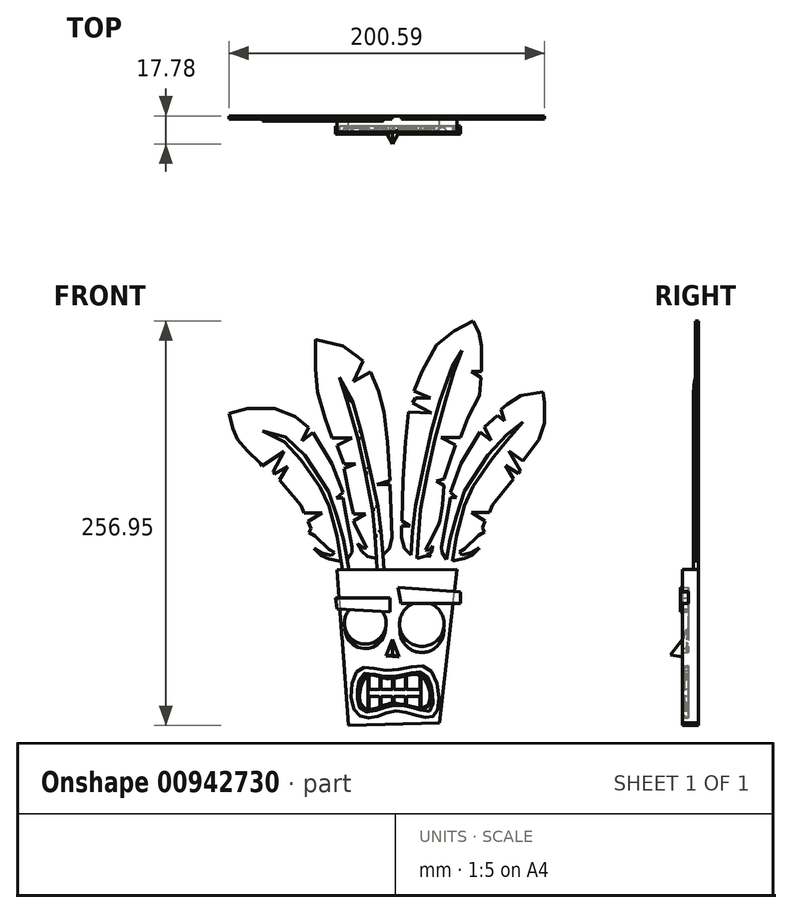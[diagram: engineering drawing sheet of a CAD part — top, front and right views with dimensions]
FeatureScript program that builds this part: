
annotation { "Feature Type Name" : "Feature", "Feature Type Description" : "" }
export const myFeature = defineFeature(function(context is Context, id is Id, definition is map)
    precondition{}
    {
        {
            var Q0;
            Q0=qCreatedBy(makeId("Front.planeOp"),FACE);
            var sketch = newSketch(context, id + "F0", { "sketchPlane" : qUnion([Q0])});
            skLineSegment(sketch, "E0", {"start": v(-33.73, 37.2) * mm, "end": v(-26.4, -61.68) * mm});
            skLineSegment(sketch, "E1", {"start": v(-26.4, -61.68) * mm, "end": v(31.35, -60.14) * mm});
            skLineSegment(sketch, "E2", {"start": v(31.35, -60.14) * mm, "end": v(42.47, 37.45) * mm});
            skLineSegment(sketch, "E3", {"start": v(42.47, 37.45) * mm, "end": v(-33.73, 37.2) * mm});
            skLineSegment(sketch, "E4", {"start": v(-30.1, 37.2) * mm, "end": v(-33.73, 58.64) * mm});
            skLineSegment(sketch, "E5", {"start": v(-33.73, 58.64) * mm, "end": v(-38.83, 77.73) * mm});
            skLineSegment(sketch, "E6", {"start": v(-38.83, 77.73) * mm, "end": v(-44.28, 90.01) * mm});
            skLineSegment(sketch, "E7", {"start": v(-44.28, 90.01) * mm, "end": v(-56.65, 107.1) * mm});
            skLineSegment(sketch, "E8", {"start": v(-56.65, 107.1) * mm, "end": v(-66.9, 118.54) * mm});
            skLineSegment(sketch, "E9", {"start": v(-66.9, 118.54) * mm, "end": v(-81.04, 125.42) * mm});
            skLineSegment(sketch, "E10", {"start": v(-81.04, 125.42) * mm, "end": v(-66.21, 121.7) * mm});
            skLineSegment(sketch, "E11", {"start": v(-66.21, 121.7) * mm, "end": v(-54.1, 109.86) * mm});
            skLineSegment(sketch, "E12", {"start": v(-54.1, 109.86) * mm, "end": v(-38.9, 87.13) * mm});
            skLineSegment(sketch, "E13", {"start": v(-38.9, 87.13) * mm, "end": v(-33.73, 71.19) * mm});
            skLineSegment(sketch, "E14", {"start": v(-33.73, 71.19) * mm, "end": v(-29.55, 56.46) * mm});
            skLineSegment(sketch, "E15", {"start": v(-29.55, 56.46) * mm, "end": v(-26, 37.22) * mm});
            skLineSegment(sketch, "E16", {"start": v(-33.73, 37.2) * mm, "end": v(42.47, 37.45) * mm, "construction": true});
            skLineSegment(sketch, "E17", {"start": v(4.37, 37.32) * mm, "end": v(4.14, 105.65) * mm, "construction": true});
            skLineSegment(sketch, "E18", {"start": v(-8.16, 37.28) * mm, "end": v(-9.36, 58.73) * mm});
            skLineSegment(sketch, "E19", {"start": v(-9.36, 58.73) * mm, "end": v(-11.04, 75.34) * mm});
            skLineSegment(sketch, "E20", {"start": v(-11.04, 75.34) * mm, "end": v(-15.42, 98.51) * mm});
            skLineSegment(sketch, "E21", {"start": v(-15.42, 98.51) * mm, "end": v(-20.28, 120.29) * mm});
            skLineSegment(sketch, "E22", {"start": v(-20.28, 120.29) * mm, "end": v(-27.17, 144.56) * mm});
            skLineSegment(sketch, "E23", {"start": v(-27.17, 144.56) * mm, "end": v(-32.03, 159.54) * mm});
            skLineSegment(sketch, "E24", {"start": v(-32.03, 159.54) * mm, "end": v(-23.71, 144.56) * mm});
            skLineSegment(sketch, "E25", {"start": v(-23.71, 144.56) * mm, "end": v(-18.3, 125.5) * mm});
            skLineSegment(sketch, "E26", {"start": v(-18.3, 125.5) * mm, "end": v(-12.9, 102.1) * mm});
            skLineSegment(sketch, "E27", {"start": v(-12.9, 102.1) * mm, "end": v(-7.76, 77.64) * mm});
            skLineSegment(sketch, "E28", {"start": v(-7.76, 77.64) * mm, "end": v(-5.82, 61.6) * mm});
            skLineSegment(sketch, "E29", {"start": v(-5.82, 61.6) * mm, "end": v(-3.76, 37.3) * mm});
            skLineSegment(sketch, "E30.MirrorCS", {"start": v(52.67, 90.34) * mm, "end": v(64.92, 107.51) * mm});
            skLineSegment(sketch, "E31.MirrorCS", {"start": v(23.74, 98.64) * mm, "end": v(28.46, 120.45) * mm});
            skLineSegment(sketch, "E32.MirrorCS", {"start": v(21.2, 102.2) * mm, "end": v(16.23, 77.72) * mm});
            skLineSegment(sketch, "E33.MirrorCS", {"start": v(17.96, 58.82) * mm, "end": v(19.52, 75.44) * mm});
            skLineSegment(sketch, "E34.MirrorCS", {"start": v(47.3, 78.02) * mm, "end": v(52.67, 90.34) * mm});
            skLineSegment(sketch, "E35.MirrorCS", {"start": v(16.23, 77.72) * mm, "end": v(14.4, 61.67) * mm});
            skLineSegment(sketch, "E36.MirrorCS", {"start": v(42.33, 58.9) * mm, "end": v(47.3, 78.02) * mm});
            skLineSegment(sketch, "E37.MirrorCS", {"start": v(19.52, 75.44) * mm, "end": v(23.74, 98.64) * mm});
            skLineSegment(sketch, "E38.MirrorCS", {"start": v(62.34, 110.25) * mm, "end": v(47.3, 87.42) * mm});
            skLineSegment(sketch, "E39.MirrorCS", {"start": v(28.46, 120.45) * mm, "end": v(35.19, 144.77) * mm});
            skLineSegment(sketch, "E40.MirrorCS", {"start": v(42.24, 71.44) * mm, "end": v(38.16, 56.68) * mm});
            skLineSegment(sketch, "E41.MirrorCS", {"start": v(31.73, 144.75) * mm, "end": v(26.45, 125.65) * mm});
            skLineSegment(sketch, "E42.MirrorCS", {"start": v(26.45, 125.65) * mm, "end": v(21.2, 102.2) * mm});
            skLineSegment(sketch, "E43.MirrorCS", {"start": v(47.3, 87.42) * mm, "end": v(42.24, 71.44) * mm});
            skLineSegment(sketch, "E44.MirrorCS", {"start": v(38.84, 37.43) * mm, "end": v(42.33, 58.9) * mm});
            skLineSegment(sketch, "E45.MirrorCS", {"start": v(38.16, 56.68) * mm, "end": v(34.74, 37.42) * mm});
            skLineSegment(sketch, "E46.MirrorCS", {"start": v(16.9, 37.36) * mm, "end": v(17.96, 58.82) * mm});
            skLineSegment(sketch, "E47.MirrorCS", {"start": v(14.4, 61.67) * mm, "end": v(12.5, 37.35) * mm});
            skLineSegment(sketch, "E48", {"start": v(-102.35, 136.45) * mm, "end": v(-99.72, 126.59) * mm});
            skLineSegment(sketch, "E49", {"start": v(-99.72, 126.59) * mm, "end": v(-96.66, 120.13) * mm});
            skLineSegment(sketch, "E50", {"start": v(-96.66, 120.13) * mm, "end": v(-90.73, 113) * mm});
            skLineSegment(sketch, "E51", {"start": v(-90.73, 113) * mm, "end": v(-82.3, 104.76) * mm});
            skLineSegment(sketch, "E52", {"start": v(-82.3, 104.76) * mm, "end": v(-81.17, 103.08) * mm});
            skLineSegment(sketch, "E53", {"start": v(-81.17, 103.08) * mm, "end": v(-67.32, 112.33) * mm});
            skLineSegment(sketch, "E54", {"start": v(-67.32, 112.33) * mm, "end": v(-74.4, 99.5) * mm});
            skLineSegment(sketch, "E55", {"start": v(-74.4, 99.5) * mm, "end": v(-73.43, 98.04) * mm});
            skLineSegment(sketch, "E56", {"start": v(-73.43, 98.04) * mm, "end": v(-65.05, 103.01) * mm});
            skLineSegment(sketch, "E57", {"start": v(-65.05, 103.01) * mm, "end": v(-70.22, 94.33) * mm});
            skLineSegment(sketch, "E58", {"start": v(-70.22, 94.33) * mm, "end": v(-56.65, 78) * mm});
            skLineSegment(sketch, "E59", {"start": v(-47.53, 58.78) * mm, "end": v(-38.6, 50.07) * mm});
            skLineSegment(sketch, "E60", {"start": v(-38.6, 50.07) * mm, "end": v(-35.37, 48.2) * mm});
            skLineSegment(sketch, "E61", {"start": v(-35.37, 48.2) * mm, "end": v(-37.05, 46.47) * mm});
            skLineSegment(sketch, "E62", {"start": v(-37.05, 46.47) * mm, "end": v(-43.38, 48.02) * mm});
            skLineSegment(sketch, "E63", {"start": v(-43.38, 48.02) * mm, "end": v(-48.26, 50.8) * mm});
            skLineSegment(sketch, "E64", {"start": v(-48.26, 50.8) * mm, "end": v(-43.68, 46.34) * mm});
            skLineSegment(sketch, "E65", {"start": v(-43.68, 46.34) * mm, "end": v(-38.6, 44.1) * mm});
            skLineSegment(sketch, "E66", {"start": v(-38.6, 44.1) * mm, "end": v(-31, 42.58) * mm});
            skLineSegment(sketch, "E67", {"start": v(-102.35, 136.45) * mm, "end": v(-90.6, 139.58) * mm});
            skLineSegment(sketch, "E68", {"start": v(-90.6, 139.58) * mm, "end": v(-73.28, 139.58) * mm});
            skLineSegment(sketch, "E69", {"start": v(-73.28, 139.58) * mm, "end": v(-60.22, 134.7) * mm});
            skLineSegment(sketch, "E70", {"start": v(-60.22, 134.7) * mm, "end": v(-51.87, 127.57) * mm});
            skLineSegment(sketch, "E71", {"start": v(-51.87, 127.57) * mm, "end": v(-55.87, 119.04) * mm});
            skLineSegment(sketch, "E72", {"start": v(-55.87, 119.04) * mm, "end": v(-48.9, 124.44) * mm});
            skLineSegment(sketch, "E73", {"start": v(-48.9, 124.44) * mm, "end": v(-36.72, 104.59) * mm});
            skLineSegment(sketch, "E74", {"start": v(-36.72, 104.59) * mm, "end": v(-29.93, 86.3) * mm});
            skLineSegment(sketch, "E75", {"start": v(-29.93, 86.3) * mm, "end": v(-33.93, 83) * mm});
            skLineSegment(sketch, "E76", {"start": v(-33.93, 83) * mm, "end": v(-29.93, 83) * mm});
            skLineSegment(sketch, "E77", {"start": v(-29.93, 83) * mm, "end": v(-28.01, 72.2) * mm});
            skLineSegment(sketch, "E78", {"start": v(-56.65, 78) * mm, "end": v(-54.63, 73.42) * mm});
            skLineSegment(sketch, "E79", {"start": v(-54.63, 73.42) * mm, "end": v(-43.22, 73.42) * mm});
            skLineSegment(sketch, "E80", {"start": v(-43.22, 73.42) * mm, "end": v(-51.93, 68.06) * mm});
            skLineSegment(sketch, "E81", {"start": v(-28.01, 72.2) * mm, "end": v(-24.22, 51.64) * mm});
            skLineSegment(sketch, "E82", {"start": v(-24.22, 51.64) * mm, "end": v(-24.22, 48.2) * mm});
            skLineSegment(sketch, "E83", {"start": v(-24.22, 48.2) * mm, "end": v(-27.16, 43.52) * mm});
            skLineSegment(sketch, "E84", {"start": v(-47.53, 58.78) * mm, "end": v(-51.56, 60.9) * mm});
            skLineSegment(sketch, "E85", {"start": v(-51.56, 60.9) * mm, "end": v(-50.22, 63.44) * mm});
            skLineSegment(sketch, "E86", {"start": v(-50.22, 63.44) * mm, "end": v(-51.93, 68.06) * mm});
            skLineSegment(sketch, "E87", {"start": v(-47.14, 183.7) * mm, "end": v(-29.93, 179.4) * mm});
            skLineSegment(sketch, "E88", {"start": v(-29.93, 179.4) * mm, "end": v(-20.26, 172.55) * mm});
            skLineSegment(sketch, "E89", {"start": v(-12.5, 163.03) * mm, "end": v(-7.3, 150.76) * mm});
            skLineSegment(sketch, "E90", {"start": v(-3.73, 137.4) * mm, "end": v(-1.54, 118.4) * mm});
            skLineSegment(sketch, "E91", {"start": v(-1.54, 118.4) * mm, "end": v(0, 94.08) * mm});
            skLineSegment(sketch, "E92", {"start": v(0, 94.08) * mm, "end": v(-8.2, 91.46) * mm});
            skLineSegment(sketch, "E93", {"start": v(-8.2, 91.46) * mm, "end": v(0, 91.46) * mm});
            skLineSegment(sketch, "E94", {"start": v(0, 91.46) * mm, "end": v(1.3, 57.73) * mm});
            skLineSegment(sketch, "E95", {"start": v(1.3, 57.73) * mm, "end": v(-0.43, 50.85) * mm});
            skLineSegment(sketch, "E96", {"start": v(-0.43, 50.85) * mm, "end": v(-4.56, 46.7) * mm});
            skLineSegment(sketch, "E97", {"start": v(-8.56, 44.51) * mm, "end": v(-14.32, 45.82) * mm});
            skLineSegment(sketch, "E98", {"start": v(-14.32, 45.82) * mm, "end": v(-17.9, 48.84) * mm});
            skLineSegment(sketch, "E99", {"start": v(-17.9, 48.84) * mm, "end": v(-20.49, 54) * mm});
            skLineSegment(sketch, "E100", {"start": v(-20.49, 54) * mm, "end": v(-16.9, 51.07) * mm});
            skLineSegment(sketch, "E101", {"start": v(-16.9, 51.07) * mm, "end": v(-14.86, 51.18) * mm});
            skLineSegment(sketch, "E102", {"start": v(-14.86, 51.18) * mm, "end": v(-18.25, 57.95) * mm});
            skLineSegment(sketch, "E103", {"start": v(-18.25, 57.95) * mm, "end": v(-22.54, 66.54) * mm});
            skLineSegment(sketch, "E104", {"start": v(-22.54, 66.54) * mm, "end": v(-23.17, 68.45) * mm});
            skLineSegment(sketch, "E105", {"start": v(-47.14, 183.7) * mm, "end": v(-47.14, 164.73) * mm});
            skLineSegment(sketch, "E106", {"start": v(-41.38, 133.7) * mm, "end": v(-36.67, 121) * mm});
            skLineSegment(sketch, "E107", {"start": v(-36.67, 121) * mm, "end": v(-24.13, 121) * mm});
            skLineSegment(sketch, "E108", {"start": v(-24.13, 121) * mm, "end": v(-33.54, 116.14) * mm});
            skLineSegment(sketch, "E109", {"start": v(-33.54, 116.14) * mm, "end": v(-29.15, 104.38) * mm});
            skLineSegment(sketch, "E110.MirrorCS", {"start": v(56.9, 51.16) * mm, "end": v(52.36, 46.66) * mm});
            skLineSegment(sketch, "E111.MirrorCS", {"start": v(32.86, 51.83) * mm, "end": v(32.89, 48.38) * mm});
            skLineSegment(sketch, "E112.MirrorCS", {"start": v(45.73, 46.75) * mm, "end": v(52.05, 48.34) * mm});
            skLineSegment(sketch, "E113.MirrorCS", {"start": v(42.37, 83.26) * mm, "end": v(38.36, 83.23) * mm});
            skLineSegment(sketch, "E114.MirrorCS", {"start": v(58.79, 63.8) * mm, "end": v(60.47, 68.44) * mm});
            skLineSegment(sketch, "E115.MirrorCS", {"start": v(52.36, 46.66) * mm, "end": v(47.3, 44.4) * mm});
            skLineSegment(sketch, "E116.MirrorCS", {"start": v(52.05, 48.34) * mm, "end": v(56.9, 51.16) * mm});
            skLineSegment(sketch, "E117.MirrorCS", {"start": v(38.34, 86.54) * mm, "end": v(42.37, 83.26) * mm});
            skLineSegment(sketch, "E118.MirrorCS", {"start": v(44.04, 48.46) * mm, "end": v(45.73, 46.75) * mm});
            skLineSegment(sketch, "E119.MirrorCS", {"start": v(65.12, 78.41) * mm, "end": v(63.13, 73.81) * mm});
            skLineSegment(sketch, "E120.MirrorCS", {"start": v(34.36, 95.01) * mm, "end": v(29.61, 93.8) * mm});
            skLineSegment(sketch, "E121.MirrorCS", {"start": v(16.2, 146.37) * mm, "end": v(14.24, 143.3) * mm});
            skLineSegment(sketch, "E122.MirrorCS", {"start": v(26.85, 58.1) * mm, "end": v(31.09, 66.72) * mm});
            skLineSegment(sketch, "E123.MirrorCS", {"start": v(64.06, 119.44) * mm, "end": v(57.06, 124.8) * mm});
            skLineSegment(sketch, "E124.MirrorCS", {"start": v(29.61, 93.8) * mm, "end": v(34.2, 90.78) * mm});
            skLineSegment(sketch, "E125.MirrorCS", {"start": v(47.25, 50.35) * mm, "end": v(44.04, 48.46) * mm});
            skLineSegment(sketch, "E126.MirrorCS", {"start": v(56.12, 59.12) * mm, "end": v(60.14, 61.28) * mm});
            skLineSegment(sketch, "E127.MirrorCS", {"start": v(82.73, 100.03) * mm, "end": v(81.76, 98.57) * mm});
            skLineSegment(sketch, "E128.MirrorCS", {"start": v(60.14, 61.28) * mm, "end": v(58.79, 63.8) * mm});
            skLineSegment(sketch, "E129.MirrorCS", {"start": v(47.3, 44.4) * mm, "end": v(39.71, 42.82) * mm});
            skLineSegment(sketch, "E130.MirrorCS", {"start": v(32.89, 48.38) * mm, "end": v(35.86, 43.73) * mm});
            skLineSegment(sketch, "E131.MirrorCS", {"start": v(9.08, 50.88) * mm, "end": v(13.23, 46.75) * mm});
            skLineSegment(sketch, "E132.MirrorCS", {"start": v(17.26, 44.6) * mm, "end": v(23, 45.95) * mm});
            skLineSegment(sketch, "E133.MirrorCS", {"start": v(31.7, 68.63) * mm, "end": v(33.27, 78.53) * mm});
            skLineSegment(sketch, "E134.MirrorCS", {"start": v(56.12, 59.12) * mm, "end": v(47.25, 50.35) * mm});
            skLineSegment(sketch, "E135.MirrorCS", {"start": v(20.39, 163.14) * mm, "end": v(15.28, 150.83) * mm});
            skLineSegment(sketch, "E136.MirrorCS", {"start": v(33.27, 78.53) * mm, "end": v(34.2, 90.78) * mm});
            skLineSegment(sketch, "E137.MirrorCS", {"start": v(15.28, 150.83) * mm, "end": v(25.86, 146.44) * mm});
            skLineSegment(sketch, "E138.MirrorCS", {"start": v(73.35, 103.48) * mm, "end": v(78.58, 94.84) * mm});
            skLineSegment(sketch, "E139.MirrorCS", {"start": v(49.47, 134) * mm, "end": v(44.85, 121.27) * mm});
            skLineSegment(sketch, "E140.MirrorCS", {"start": v(60, 127.95) * mm, "end": v(64.06, 119.44) * mm});
            skLineSegment(sketch, "E141.MirrorCS", {"start": v(32.3, 121.19) * mm, "end": v(41.75, 116.4) * mm});
            skLineSegment(sketch, "E142.MirrorCS", {"start": v(78.58, 94.84) * mm, "end": v(65.12, 78.41) * mm});
            skLineSegment(sketch, "E143.MirrorCS", {"start": v(63.13, 73.81) * mm, "end": v(51.71, 73.73) * mm});
            skLineSegment(sketch, "E144.MirrorCS", {"start": v(11.8, 137.45) * mm, "end": v(9.73, 118.45) * mm});
            skLineSegment(sketch, "E145.MirrorCS", {"start": v(37.43, 104.6) * mm, "end": v(34.36, 95.01) * mm});
            skLineSegment(sketch, "E146.MirrorCS", {"start": v(14.24, 143.3) * mm, "end": v(26.4, 136.88) * mm});
            skLineSegment(sketch, "E147.MirrorCS", {"start": v(81.76, 98.57) * mm, "end": v(73.35, 103.48) * mm});
            skLineSegment(sketch, "E148.MirrorCS", {"start": v(44.85, 121.27) * mm, "end": v(32.3, 121.19) * mm});
            skLineSegment(sketch, "E149.MirrorCS", {"start": v(51.71, 73.73) * mm, "end": v(60.47, 68.44) * mm});
            skLineSegment(sketch, "E150.MirrorCS", {"start": v(31.09, 66.72) * mm, "end": v(31.7, 68.63) * mm});
            skLineSegment(sketch, "E151.MirrorCS", {"start": v(38.36, 83.23) * mm, "end": v(36.52, 72.42) * mm});
            skLineSegment(sketch, "E152.MirrorCS", {"start": v(41.75, 116.4) * mm, "end": v(37.43, 104.6) * mm});
            skLineSegment(sketch, "E153.MirrorCS", {"start": v(36.52, 72.42) * mm, "end": v(32.86, 51.83) * mm});
            skLineSegment(sketch, "E154.MirrorCS", {"start": v(26.4, 136.88) * mm, "end": v(11.8, 137.45) * mm});
            skLineSegment(sketch, "E155.MirrorCS", {"start": v(9.73, 118.45) * mm, "end": v(8.36, 94.1) * mm});
            skLineSegment(sketch, "E156.MirrorCS", {"start": v(57.06, 124.8) * mm, "end": v(45, 104.86) * mm});
            skLineSegment(sketch, "E157.MirrorCS", {"start": v(56.71, 148.05) * mm, "end": v(49.47, 134) * mm});
            skLineSegment(sketch, "E158.MirrorCS", {"start": v(75.56, 112.81) * mm, "end": v(82.73, 100.03) * mm});
            skLineSegment(sketch, "E159.MirrorCS", {"start": v(25.86, 146.44) * mm, "end": v(16.2, 146.37) * mm});
            skLineSegment(sketch, "E160.MirrorCS", {"start": v(45, 104.86) * mm, "end": v(38.34, 86.54) * mm});
            skLineSegment(sketch, "E161.MirrorCS", {"start": v(68.3, 135.14) * mm, "end": v(60, 127.95) * mm});
            skLineSegment(sketch, "E162.MirrorCS", {"start": v(7.31, 57.75) * mm, "end": v(9.08, 50.88) * mm});
            skLineSegment(sketch, "E163", {"start": v(20.39, 163.14) * mm, "end": v(29.6, 179.9) * mm});
            skLineSegment(sketch, "E164", {"start": v(29.6, 179.9) * mm, "end": v(40.5, 188.84) * mm});
            skLineSegment(sketch, "E165", {"start": v(40.5, 188.84) * mm, "end": v(52.8, 195.27) * mm});
            skLineSegment(sketch, "E166", {"start": v(58.1, 179.34) * mm, "end": v(58.1, 163.14) * mm});
            skLineSegment(sketch, "E167", {"start": v(58.1, 163.14) * mm, "end": v(51.68, 163.14) * mm});
            skLineSegment(sketch, "E168", {"start": v(51.68, 163.14) * mm, "end": v(57.83, 159.5) * mm});
            skLineSegment(sketch, "E169", {"start": v(57.83, 159.5) * mm, "end": v(56.71, 148.05) * mm});
            skLineSegment(sketch, "E170", {"start": v(-41.38, 133.7) * mm, "end": v(-46.11, 150.28) * mm});
            skLineSegment(sketch, "E171", {"start": v(-46.11, 150.28) * mm, "end": v(-47.14, 164.73) * mm});
            skLineSegment(sketch, "E172", {"start": v(58.1, 179.34) * mm, "end": v(56.57, 188) * mm});
            skLineSegment(sketch, "E173", {"start": v(56.57, 188) * mm, "end": v(52.8, 195.27) * mm});
            skLineSegment(sketch, "E174", {"start": v(31.73, 144.75) * mm, "end": v(39.43, 166.12) * mm});
            skLineSegment(sketch, "E175", {"start": v(39.43, 166.12) * mm, "end": v(45.76, 176.67) * mm});
            skLineSegment(sketch, "E176", {"start": v(45.76, 176.67) * mm, "end": v(40.75, 163.14) * mm});
            skLineSegment(sketch, "E177", {"start": v(40.75, 163.14) * mm, "end": v(35.19, 144.77) * mm});
            skLineSegment(sketch, "E178", {"start": v(75.56, 112.81) * mm, "end": v(84.53, 106.25) * mm});
            skLineSegment(sketch, "E179", {"start": v(84.53, 106.25) * mm, "end": v(94.55, 119.94) * mm});
            skLineSegment(sketch, "E180", {"start": v(94.55, 119.94) * mm, "end": v(98.24, 130.51) * mm});
            skLineSegment(sketch, "E181", {"start": v(98.24, 130.51) * mm, "end": v(98.24, 143.43) * mm});
            skLineSegment(sketch, "E182", {"start": v(98.24, 143.43) * mm, "end": v(97.27, 150.11) * mm});
            skLineSegment(sketch, "E183", {"start": v(97.27, 150.11) * mm, "end": v(83.1, 148.05) * mm});
            skLineSegment(sketch, "E184", {"start": v(83.1, 148.05) * mm, "end": v(74.2, 142.35) * mm});
            skLineSegment(sketch, "E185", {"start": v(74.2, 142.35) * mm, "end": v(70.43, 139.02) * mm});
            skLineSegment(sketch, "E186", {"start": v(70.43, 139.02) * mm, "end": v(72.65, 131.82) * mm});
            skLineSegment(sketch, "E187", {"start": v(72.65, 131.82) * mm, "end": v(68.3, 135.14) * mm});
            skLineSegment(sketch, "E188", {"start": v(62.34, 110.25) * mm, "end": v(74.2, 123.28) * mm});
            skLineSegment(sketch, "E189", {"start": v(74.2, 123.28) * mm, "end": v(84.52, 131.04) * mm});
            skLineSegment(sketch, "E190", {"start": v(84.52, 131.04) * mm, "end": v(74.2, 119.5) * mm});
            skLineSegment(sketch, "E191", {"start": v(74.2, 119.5) * mm, "end": v(64.92, 107.51) * mm});
            skLineSegment(sketch, "E192", {"start": v(8.36, 94.1) * mm, "end": v(7.53, 68.37) * mm});
            skLineSegment(sketch, "E193", {"start": v(7.53, 68.37) * mm, "end": v(12.65, 65.19) * mm});
            skLineSegment(sketch, "E194", {"start": v(12.65, 65.19) * mm, "end": v(7.3, 65.17) * mm});
            skLineSegment(sketch, "E195", {"start": v(7.3, 65.17) * mm, "end": v(7.31, 57.75) * mm});
            skLineSegment(sketch, "E196", {"start": v(-29.15, 104.38) * mm, "end": v(-21.93, 104.38) * mm});
            skLineSegment(sketch, "E197", {"start": v(-21.93, 104.38) * mm, "end": v(-29.15, 101.63) * mm});
            skLineSegment(sketch, "E198", {"start": v(-29.15, 101.63) * mm, "end": v(-25.8, 83.95) * mm});
            skLineSegment(sketch, "E199", {"start": v(-25.8, 83.95) * mm, "end": v(-23.33, 72.63) * mm});
            skLineSegment(sketch, "E200", {"start": v(-23.33, 72.63) * mm, "end": v(-15.42, 72.63) * mm});
            skLineSegment(sketch, "E201", {"start": v(-15.42, 72.63) * mm, "end": v(-23.17, 68.45) * mm});
            skLineSegment(sketch, "E202", {"start": v(-3.73, 137.4) * mm, "end": v(-7.3, 150.76) * mm});
            skLineSegment(sketch, "E203", {"start": v(-12.5, 163.03) * mm, "end": v(-23.31, 156.9) * mm});
            skLineSegment(sketch, "E204", {"start": v(-23.31, 156.9) * mm, "end": v(-17.26, 169.77) * mm});
            skLineSegment(sketch, "E205", {"start": v(-17.26, 169.77) * mm, "end": v(-20.26, 172.55) * mm});
            skLineSegment(sketch, "E206", {"start": v(26.85, 58.1) * mm, "end": v(22.54, 49.96) * mm});
            skLineSegment(sketch, "E207", {"start": v(22.54, 49.96) * mm, "end": v(23.46, 49.47) * mm});
            skLineSegment(sketch, "E208", {"start": v(23.46, 49.47) * mm, "end": v(25.53, 50.27) * mm});
            skLineSegment(sketch, "E209", {"start": v(25.53, 50.27) * mm, "end": v(27.12, 52.37) * mm});
            skLineSegment(sketch, "E210", {"start": v(27.12, 52.37) * mm, "end": v(26.57, 48.98) * mm});
            skLineSegment(sketch, "E211", {"start": v(23, 45.95) * mm, "end": v(25.05, 45.95) * mm});
            skLineSegment(sketch, "E212", {"start": v(25.05, 45.95) * mm, "end": v(26.03, 45.66) * mm});
            skLineSegment(sketch, "E213", {"start": v(26.03, 45.66) * mm, "end": v(25.05, 46.55) * mm});
            skLineSegment(sketch, "E214", {"start": v(25.05, 46.55) * mm, "end": v(23.66, 46.98) * mm});
            skLineSegment(sketch, "E215", {"start": v(23.66, 46.98) * mm, "end": v(25.36, 47.78) * mm});
            skLineSegment(sketch, "E216", {"start": v(25.36, 47.78) * mm, "end": v(26.57, 48.98) * mm});
            skSolve(sketch);
        }
        {
            var Q0;
            Q0=makeQuery(id+"F0.imprint","IMPRINT",FACE,{"disambiguationData":[TD([[makeQuery(id+"F0.imprint","IMPRINT",EDGE,{"derivedFrom":sQuery(id+"F0.wireOp",EDGE,"E0")}),1.0]])]});
            extrude(context, id + "F1", {"entities" : qUnion([Q0]), "depth" : 6.35 * mm, "offsetDistance" : 25.4 * mm});
        }
        {
            var Q0;
            Q0=makeQuery(id+"F0.imprint","IMPRINT",FACE,{"disambiguationData":[TD([[makeQuery(id+"F0.imprint","IMPRINT",EDGE,{"derivedFrom":sQuery(id+"F0.wireOp",EDGE,"E0")}),1.0]])]});
            extrude(context, id + "F2", {"entities" : qUnion([Q0]), "depth" : 6.35 * mm, "offsetDistance" : 25.4 * mm});
        }
        {
            var Q0;
            Q0=makeQuery(id+"F1.opExtrude","CAP_FACE",FACE,{"disambiguationData":[OSD([sQuery(id+"F0.wireOp",EDGE,"E0"),sQuery(id+"F0.wireOp",EDGE,"E1"),sQuery(id+"F0.wireOp",EDGE,"E2"),sQuery(id+"F0.wireOp",EDGE,"E3")])],"isStart":false});
            var sketch = newSketch(context, id + "F3", { "sketchPlane" : qUnion([Q0])});
            skLineSegment(sketch, "E217", {"start": v(-34.59, 19.33) * mm, "end": v(0, 19.33) * mm});
            skLineSegment(sketch, "E218", {"start": v(0, 19.33) * mm, "end": v(0, 10.57) * mm});
            skLineSegment(sketch, "E219", {"start": v(0, 10.57) * mm, "end": v(-33.73, 12.37) * mm});
            skLineSegment(sketch, "E220", {"start": v(-33.73, 12.37) * mm, "end": v(-34.59, 19.33) * mm});
            skLineSegment(sketch, "E221", {"start": v(5.03, 25.97) * mm, "end": v(6.96, 15.82) * mm});
            skLineSegment(sketch, "E222", {"start": v(6.96, 15.82) * mm, "end": v(44.74, 15.82) * mm});
            skLineSegment(sketch, "E223", {"start": v(44.74, 15.82) * mm, "end": v(44.74, 23.34) * mm});
            skLineSegment(sketch, "E224", {"start": v(44.74, 23.34) * mm, "end": v(5.03, 25.97) * mm});
            skArc(sketch, "E225", {"start": v(-25.8, 11.95) * mm, "mid": v(-16.41, -9.85) * mm, "end": v(-4.77, 10.83) * mm});
            skArc(sketch, "E226", {"start": v(14.65, 15.82) * mm, "mid": v(20.25, -11.32) * mm, "end": v(25.85, 15.82) * mm});
            skArc(sketch, "E227", {"start": v(-28.5, 0) * mm, "mid": v(-15.7, -12.78) * mm, "end": v(-2.91, 0) * mm});
            skArc(sketch, "E228", {"start": v(6.39, 0) * mm, "mid": v(20.25, -15.24) * mm, "end": v(34.12, 0) * mm});
            skFitSpline(sketch, "E229", {"points": [v(-22.95, -51.39) * mm, v(-19.58, -26) * mm, v(0, -26.74) * mm, v(24.32, -25.37) * mm, v(30.05, -52.4) * mm, v(22.2, -56.35) * mm, v(3.88, -52.46) * mm, v(-11.38, -56.64) * mm, v(-22.95, -51.39) * mm]});
            skFitSpline(sketch, "E230", {"points": [v(-18.64, -47.6) * mm, v(-14.13, -30.08) * mm, v(0, -32.12) * mm, v(19.96, -30.15) * mm, v(23.88, -49.13) * mm, v(2.95, -47.38) * mm, v(-10.8, -51.39) * mm, v(-18.64, -47.6) * mm]});
            skPoint(sketch, "E231.endSnap0", {"position": v(19.13, -18.04) * mm});
            skSolve(sketch);
        }
        {
            var Q0;
            {var subQ4=sQuery(id+"F3.wireOp",EDGE,"E218");Q0=makeQuery(id+"F3.imprint","IMPRINT",FACE,{"disambiguationData":[TD([[makeQuery(id+"F3.imprint","IMPRINT",EDGE,{"derivedFrom":subQ4}),-1.0]])]});}
            var Q1;
            {var subQ0=sQuery(id+"F3.wireOp",EDGE,"E220");Q1=makeQuery(id+"F3.imprint","IMPRINT",FACE,{"disambiguationData":[TD([[makeQuery(id+"F3.imprint","IMPRINT",EDGE,{"derivedFrom":subQ0}),-1.0]])]});}
            var Q2;
            {var subQ6=sQuery(id+"F3.wireOp",EDGE,"E221");Q2=makeQuery(id+"F3.imprint","IMPRINT",FACE,{"disambiguationData":[TD([[makeQuery(id+"F3.imprint","IMPRINT",EDGE,{"derivedFrom":subQ6}),1.0]])]});}
            var Q3;
            {var subQ0=sQuery(id+"F3.wireOp",EDGE,"E223");Q3=makeQuery(id+"F3.imprint","IMPRINT",FACE,{"disambiguationData":[TD([[makeQuery(id+"F3.imprint","IMPRINT",EDGE,{"derivedFrom":subQ0}),1.0]])]});}
            extrude(context, id + "F4", {"entities" : qUnion([Q0, Q1, Q2, Q3]), "depth" : 5.08 * mm, "offsetDistance" : 25.4 * mm});
        }
        {
            var Q0;
            {var subQ0=sQuery(id+"F3.wireOp",EDGE,"E225");var subQ1=sQuery(id+"F3.wireOp",EDGE,"E219");var subQ2=makeQuery(id+"F3.imprint","INTERSECT",VERTEX,{"disambiguationData":[OD(0.0)],"derivedFrom":[subQ1,subQ0]});Q0=makeQuery(id+"F3.imprint","IMPRINT",FACE,{"disambiguationData":[TD([[makeQuery(id+"F3.imprint","IMPRINT",EDGE,{"disambiguationData":[TD([[subQ2,1.0]])],"derivedFrom":subQ1}),1.0]])]});}
            var Q1;
            {var subQ0=sQuery(id+"F3.wireOp",EDGE,"E226");var subQ1=sQuery(id+"F3.wireOp",EDGE,"E222");var subQ2=makeQuery(id+"F3.imprint","INTERSECT",VERTEX,{"disambiguationData":[OD(0.0)],"derivedFrom":[subQ1,subQ0]});Q1=makeQuery(id+"F3.imprint","IMPRINT",FACE,{"disambiguationData":[TD([[makeQuery(id+"F3.imprint","IMPRINT",EDGE,{"disambiguationData":[TD([[subQ2,-1.0]])],"derivedFrom":subQ1}),-1.0]])]});}
            extrude(context, id + "F5", {"entities" : qUnion([Q0, Q1]), "depth" : 3.8 * mm, "offsetDistance" : 25.4 * mm});
        }
        {
            var Q0;
            Q0=makeQuery(id+"F5.opExtrude","CAP_EDGE",EDGE,{"disambiguationData":[OSD([sQuery(id+"F3.wireOp",EDGE,"E226")])],"isStart":false});
            var Q1;
            Q1=makeQuery(id+"F5.opExtrude","CAP_EDGE",EDGE,{"disambiguationData":[OSD([sQuery(id+"F3.wireOp",EDGE,"E225")])],"isStart":false});
            fillet(context, id + "F6", {"entities" : qUnion([Q0, Q1]), "radius" : 3.8 * mm, "tangentPropagation" : true, "allowEdgeOverflow" : false});
        }
        {
            var Q0;
            {var subQ0=sQuery(id+"F3.wireOp",EDGE,"E227");Q0=makeQuery(id+"F3.imprint","IMPRINT",FACE,{"disambiguationData":[TD([[makeQuery(id+"F3.imprint","IMPRINT",EDGE,{"derivedFrom":subQ0}),1.0]])]});}
            var Q1;
            {var subQ0=sQuery(id+"F3.wireOp",EDGE,"E228");Q1=makeQuery(id+"F3.imprint","IMPRINT",FACE,{"disambiguationData":[TD([[makeQuery(id+"F3.imprint","IMPRINT",EDGE,{"derivedFrom":subQ0}),1.0]])]});}
            extrude(context, id + "F7", {"entities" : qUnion([Q0, Q1]), "depth" : 1.27 * mm, "offsetDistance" : 25.4 * mm});
        }
        {
            var Q0;
            Q0=makeQuery(id+"F7.opExtrude","CAP_EDGE",EDGE,{"disambiguationData":[OSD([sQuery(id+"F3.wireOp",EDGE,"E228")])],"isStart":false});
            var Q1;
            Q1=makeQuery(id+"F7.opExtrude","CAP_EDGE",EDGE,{"disambiguationData":[OSD([sQuery(id+"F3.wireOp",EDGE,"E226")])],"isStart":false});
            var Q2;
            Q2=makeQuery(id+"F7.opExtrude","CAP_EDGE",EDGE,{"disambiguationData":[OSD([sQuery(id+"F3.wireOp",EDGE,"E225")])],"isStart":false});
            var Q3;
            Q3=makeQuery(id+"F7.opExtrude","CAP_EDGE",EDGE,{"disambiguationData":[OSD([sQuery(id+"F3.wireOp",EDGE,"E227")])],"isStart":false});
            fillet(context, id + "F8", {"entities" : qUnion([Q0, Q1, Q2, Q3]), "radius" : 1.27 * mm, "tangentPropagation" : true, "allowEdgeOverflow" : false});
        }
        {
            var Q0;
            Q0=makeQuery(id+"F3.imprint","IMPRINT",FACE,{"disambiguationData":[TD([[makeQuery(id+"F3.imprint","IMPRINT",EDGE,{"derivedFrom":sQuery(id+"F3.wireOp",EDGE,"E230")}),1.0]])]});
            extrude(context, id + "F9", {"entities" : qUnion([Q0]), "depth" : 3.8 * mm, "offsetDistance" : 25.4 * mm});
        }
        {
            var Q0;
            Q0=makeQuery(id+"F9.opExtrude","CAP_EDGE",EDGE,{"disambiguationData":[OSD([sQuery(id+"F3.wireOp",EDGE,"E229")])],"isStart":false});
            fillet(context, id + "F10", {"entities" : qUnion([Q0]), "radius" : 3.8 * mm, "tangentPropagation" : true, "allowEdgeOverflow" : false});
        }
        {
            var Q0;
            Q0=makeQuery(id+"F9.opExtrude","CAP_EDGE",EDGE,{"disambiguationData":[OSD([sQuery(id+"F3.wireOp",EDGE,"E230")])],"isStart":false});
            fillet(context, id + "F11", {"entities" : qUnion([Q0]), "radius" : 0.5 * mm, "tangentPropagation" : true, "allowEdgeOverflow" : false});
        }
        {
            var Q0;
            {var subQ0=sQuery(id+"F3.wireOp",EDGE,"jRf8W3L5-f59u-6WBQ-xMSF-ZkOYL2fi1t1x");var subQ1=sQuery(id+"F3.wireOp",EDGE,"E230");var subQ2=makeQuery(id+"F3.imprint","INTERSECT",VERTEX,{"disambiguationData":[OD(0.0)],"derivedFrom":[subQ1,subQ0]});Q0=makeQuery(id+"F3.imprint","IMPRINT",FACE,{"disambiguationData":[TD([[makeQuery(id+"F3.imprint","IMPRINT",EDGE,{"disambiguationData":[TD([[subQ2,1.0]])],"derivedFrom":subQ1}),-1.0]])]});}
            var Q1;
            {var subQ0=sQuery(id+"F3.wireOp",EDGE,"NiSHTitp-dRbf-uryj-5PHh-8nDeX1NtHp2X");var subQ1=sQuery(id+"F3.wireOp",EDGE,"E230");var subQ2=makeQuery(id+"F3.imprint","INTERSECT",VERTEX,{"disambiguationData":[OD(0.0)],"derivedFrom":[subQ1,subQ0]});Q1=makeQuery(id+"F3.imprint","IMPRINT",FACE,{"disambiguationData":[TD([[makeQuery(id+"F3.imprint","IMPRINT",EDGE,{"disambiguationData":[TD([[subQ2,1.0]])],"derivedFrom":subQ1}),-1.0]])]});}
            var Q2;
            {var subQ0=sQuery(id+"F3.wireOp",EDGE,"sOFvxX6n-Jmxv-Fggd-zCcz-dTaaUDqK9s0u");var subQ1=sQuery(id+"F3.wireOp",EDGE,"E230");var subQ2=makeQuery(id+"F3.imprint","INTERSECT",VERTEX,{"disambiguationData":[OD(0.0)],"derivedFrom":[subQ1,subQ0]});Q2=makeQuery(id+"F3.imprint","IMPRINT",FACE,{"disambiguationData":[TD([[makeQuery(id+"F3.imprint","IMPRINT",EDGE,{"disambiguationData":[TD([[subQ2,1.0]])],"derivedFrom":subQ1}),-1.0]])]});}
            var Q3;
            {var subQ0=sQuery(id+"F3.wireOp",EDGE,"sOFvxX6n-Jmxv-Fggd-zCcz-dTaaUDqK9s0u");var subQ1=sQuery(id+"F3.wireOp",EDGE,"E230");var subQ2=makeQuery(id+"F3.imprint","INTERSECT",VERTEX,{"disambiguationData":[OD(0.0)],"derivedFrom":[subQ1,subQ0]});Q3=makeQuery(id+"F3.imprint","IMPRINT",FACE,{"disambiguationData":[TD([[makeQuery(id+"F3.imprint","IMPRINT",EDGE,{"disambiguationData":[TD([[subQ2,-1.0]])],"derivedFrom":subQ1}),-1.0]])]});}
            var Q4;
            {var subQ0=sQuery(id+"F3.wireOp",EDGE,"txAUoQJX-vEQ5-siAy-kIKD-OxslCe6YKnOs");var subQ1=sQuery(id+"F3.wireOp",EDGE,"E230");var subQ2=makeQuery(id+"F3.imprint","INTERSECT",VERTEX,{"disambiguationData":[OD(0.0)],"derivedFrom":[subQ1,subQ0]});Q4=makeQuery(id+"F3.imprint","IMPRINT",FACE,{"disambiguationData":[TD([[makeQuery(id+"F3.imprint","IMPRINT",EDGE,{"disambiguationData":[TD([[subQ2,-1.0]])],"derivedFrom":subQ1}),-1.0]])]});}
            var Q5;
            {var subQ0=sQuery(id+"F3.wireOp",EDGE,"cpWfK3jz-DfX8-C3p2-WDs1-wr6fSfQ65gwf");var subQ1=sQuery(id+"F3.wireOp",EDGE,"E230");var subQ2=makeQuery(id+"F3.imprint","INTERSECT",VERTEX,{"disambiguationData":[OD(0.0)],"derivedFrom":[subQ1,subQ0]});Q5=makeQuery(id+"F3.imprint","IMPRINT",FACE,{"disambiguationData":[TD([[makeQuery(id+"F3.imprint","IMPRINT",EDGE,{"disambiguationData":[TD([[subQ2,-1.0]])],"derivedFrom":subQ1}),-1.0]])]});}
            var Q6;
            {var subQ0=sQuery(id+"F3.wireOp",EDGE,"jRf8W3L5-f59u-6WBQ-xMSF-ZkOYL2fi1t1x");var subQ1=sQuery(id+"F3.wireOp",EDGE,"E230");var subQ2=makeQuery(id+"F3.imprint","INTERSECT",VERTEX,{"disambiguationData":[OD(1.0)],"derivedFrom":[subQ1,subQ0]});Q6=makeQuery(id+"F3.imprint","IMPRINT",FACE,{"disambiguationData":[TD([[makeQuery(id+"F3.imprint","IMPRINT",EDGE,{"disambiguationData":[TD([[subQ2,-1.0]])],"derivedFrom":subQ1}),-1.0]])]});}
            var Q7;
            {var subQ0=sQuery(id+"F3.wireOp",EDGE,"NiSHTitp-dRbf-uryj-5PHh-8nDeX1NtHp2X");var subQ1=sQuery(id+"F3.wireOp",EDGE,"E230");var subQ2=makeQuery(id+"F3.imprint","INTERSECT",VERTEX,{"disambiguationData":[OD(1.0)],"derivedFrom":[subQ1,subQ0]});Q7=makeQuery(id+"F3.imprint","IMPRINT",FACE,{"disambiguationData":[TD([[makeQuery(id+"F3.imprint","IMPRINT",EDGE,{"disambiguationData":[TD([[subQ2,-1.0]])],"derivedFrom":subQ1}),-1.0]])]});}
            var Q8;
            {var subQ0=sQuery(id+"F3.wireOp",EDGE,"sOFvxX6n-Jmxv-Fggd-zCcz-dTaaUDqK9s0u");var subQ1=sQuery(id+"F3.wireOp",EDGE,"E230");var subQ2=makeQuery(id+"F3.imprint","INTERSECT",VERTEX,{"disambiguationData":[OD(1.0)],"derivedFrom":[subQ1,subQ0]});Q8=makeQuery(id+"F3.imprint","IMPRINT",FACE,{"disambiguationData":[TD([[makeQuery(id+"F3.imprint","IMPRINT",EDGE,{"disambiguationData":[TD([[subQ2,-1.0]])],"derivedFrom":subQ1}),-1.0]])]});}
            var Q9;
            {var subQ0=sQuery(id+"F3.wireOp",EDGE,"sOFvxX6n-Jmxv-Fggd-zCcz-dTaaUDqK9s0u");var subQ1=sQuery(id+"F3.wireOp",EDGE,"E230");var subQ2=makeQuery(id+"F3.imprint","INTERSECT",VERTEX,{"disambiguationData":[OD(1.0)],"derivedFrom":[subQ1,subQ0]});Q9=makeQuery(id+"F3.imprint","IMPRINT",FACE,{"disambiguationData":[TD([[makeQuery(id+"F3.imprint","IMPRINT",EDGE,{"disambiguationData":[TD([[subQ2,1.0]])],"derivedFrom":subQ1}),-1.0]])]});}
            var Q10;
            {var subQ0=sQuery(id+"F3.wireOp",EDGE,"txAUoQJX-vEQ5-siAy-kIKD-OxslCe6YKnOs");var subQ1=sQuery(id+"F3.wireOp",EDGE,"E230");var subQ2=makeQuery(id+"F3.imprint","INTERSECT",VERTEX,{"disambiguationData":[OD(1.0)],"derivedFrom":[subQ1,subQ0]});Q10=makeQuery(id+"F3.imprint","IMPRINT",FACE,{"disambiguationData":[TD([[makeQuery(id+"F3.imprint","IMPRINT",EDGE,{"disambiguationData":[TD([[subQ2,1.0]])],"derivedFrom":subQ1}),-1.0]])]});}
            var Q11;
            {var subQ0=sQuery(id+"F3.wireOp",EDGE,"cpWfK3jz-DfX8-C3p2-WDs1-wr6fSfQ65gwf");var subQ1=sQuery(id+"F3.wireOp",EDGE,"E230");var subQ2=makeQuery(id+"F3.imprint","INTERSECT",VERTEX,{"disambiguationData":[OD(1.0)],"derivedFrom":[subQ1,subQ0]});Q11=makeQuery(id+"F3.imprint","IMPRINT",FACE,{"disambiguationData":[TD([[makeQuery(id+"F3.imprint","IMPRINT",EDGE,{"disambiguationData":[TD([[subQ2,1.0]])],"derivedFrom":subQ1}),-1.0]])]});}
            extrude(context, id + "F12", {"entities" : qUnion([Q0, Q1, Q2, Q3, Q4, Q5, Q6, Q7, Q8, Q9, Q10, Q11]), "depth" : 2.54 * mm, "offsetDistance" : 25.4 * mm});
        }
        {
            var Q0;
            {var subQ11=sQuery(id+"F3.wireOp",EDGE,"E218");Q0=makeQuery(id+"F3.imprint","IMPRINT",FACE,{"disambiguationData":[TD([[makeQuery(id+"F3.imprint","IMPRINT",EDGE,{"derivedFrom":subQ11}),1.0]])]});}
            cPlane(context, id + "F13", {"entities" : qUnion([Q0]), "cplaneType" : CPlaneType.OFFSET, "offset" : 11.43 * mm, "width" : 152.4 * mm, "height" : 152.4 * mm});
        }
        {
            var Q0;
            Q0=qCreatedBy(id+"F13.planeOp",FACE);
            var sketch = newSketch(context, id + "F14", { "sketchPlane" : qUnion([Q0])});
            skPoint(sketch, "E232", {"position": v(1.7, -16.89) * mm});
            skSolve(sketch);
        }
        {
            var Q0;
            {var subQ11=sQuery(id+"F3.wireOp",EDGE,"E218");Q0=makeQuery(id+"F3.imprint","IMPRINT",FACE,{"disambiguationData":[TD([[makeQuery(id+"F3.imprint","IMPRINT",EDGE,{"derivedFrom":subQ11}),1.0]])]});}
            var sketch = newSketch(context, id + "F15", { "sketchPlane" : qUnion([Q0])});
            skLineSegment(sketch, "E233", {"start": v(1.7, -2.06) * mm, "end": v(-4.5, -17.8) * mm});
            skLineSegment(sketch, "E234", {"start": v(-4.5, -17.8) * mm, "end": v(7.67, -18.63) * mm});
            skLineSegment(sketch, "E235", {"start": v(7.67, -18.63) * mm, "end": v(1.7, -2.06) * mm});
            skSolve(sketch);
        }
        {
            var Q1;
            Q1=makeQuery(id+"F15.imprint","IMPRINT",FACE,{"disambiguationData":[TD([[makeQuery(id+"F15.imprint","IMPRINT",EDGE,{"derivedFrom":sQuery(id+"F15.wireOp",EDGE,"E233")}),1.0]])]});
            var Q2;
            Q2=sQuery(id+"F14.wireOp",VERTEX,"E232");
            loft(context, id + "F16", {"operationType" : NewBodyOperationType.ADD, "sheetProfilesArray" : [{ "sheetProfileEntities" : qUnion([Q1]) }, { "sheetProfileEntities" : qUnion([Q2]) }]});
        }
        {
            var Q0;
            Q0=makeQuery(id+"F12.opExtrude","CAP_FACE",FACE,{"disambiguationData":[OSD([sQuery(id+"F3.wireOp",EDGE,"E230")])],"isStart":false});
            var sketch = newSketch(context, id + "F17", { "sketchPlane" : qUnion([Q0])});
            skLineSegment(sketch, "E236", {"start": v(-18.82, -38.83) * mm, "end": v(25, -38.83) * mm});
            skLineSegment(sketch, "E237", {"start": v(-19.3, -43.25) * mm, "end": v(25.58, -43.25) * mm});
            skLineSegment(sketch, "E238", {"start": v(1.71, -38.83) * mm, "end": v(1.71, -32.03) * mm});
            skLineSegment(sketch, "E239", {"start": v(1.71, -38.83) * mm, "end": v(1.71, -47.4) * mm});
            skLineSegment(sketch, "E240", {"start": v(2.47, -47.38) * mm, "end": v(2.47, -31.94) * mm});
            skLineSegment(sketch, "E241", {"start": v(9.9, -30.07) * mm, "end": v(9.9, -48.55) * mm});
            skLineSegment(sketch, "E242", {"start": v(10.5, -48.7) * mm, "end": v(10.5, -29.9) * mm});
            skLineSegment(sketch, "E243", {"start": v(19.14, -29.7) * mm, "end": v(19.14, -50.45) * mm});
            skLineSegment(sketch, "E244", {"start": v(19.84, -50.47) * mm, "end": v(19.84, -30.08) * mm});
            skLineSegment(sketch, "E245", {"start": v(-5.72, -30.99) * mm, "end": v(-5.72, -49.52) * mm});
            skLineSegment(sketch, "E246", {"start": v(-6.44, -30.75) * mm, "end": v(-6.44, -49.84) * mm});
            skLineSegment(sketch, "E247", {"start": v(-13.3, -29.7) * mm, "end": v(-13.3, -51.53) * mm});
            skLineSegment(sketch, "E248", {"start": v(-13.98, -30) * mm, "end": v(-13.98, -51.44) * mm});
            skSolve(sketch);
        }
        {
            var Q0;
            {var subQ0=sQuery(id+"F17.wireOp",EDGE,"E248");var subQ1=sQuery(id+"F17.wireOp",EDGE,"E236");var subQ2=makeQuery(id+"F17.imprint","INTERSECT",VERTEX,{"derivedFrom":[subQ1,subQ0]});Q0=makeQuery(id+"F17.imprint","IMPRINT",FACE,{"disambiguationData":[TD([[makeQuery(id+"F17.imprint","IMPRINT",EDGE,{"disambiguationData":[TD([[subQ2,-1.0]])],"derivedFrom":subQ1}),1.0]])]});}
            var Q1;
            {var subQ0=sQuery(id+"F17.wireOp",EDGE,"E248");var subQ1=sQuery(id+"F17.wireOp",EDGE,"E236");var subQ2=makeQuery(id+"F17.imprint","INTERSECT",VERTEX,{"derivedFrom":[subQ1,subQ0]});Q1=makeQuery(id+"F17.imprint","IMPRINT",FACE,{"disambiguationData":[TD([[makeQuery(id+"F17.imprint","IMPRINT",EDGE,{"disambiguationData":[TD([[subQ2,-1.0]])],"derivedFrom":subQ1}),-1.0]])]});}
            var Q2;
            {var subQ0=sQuery(id+"F17.wireOp",EDGE,"E247");var subQ1=sQuery(id+"F17.wireOp",EDGE,"E236");var subQ2=makeQuery(id+"F17.imprint","INTERSECT",VERTEX,{"derivedFrom":[subQ1,subQ0]});Q2=makeQuery(id+"F17.imprint","IMPRINT",FACE,{"disambiguationData":[TD([[makeQuery(id+"F17.imprint","IMPRINT",EDGE,{"disambiguationData":[TD([[subQ2,-1.0]])],"derivedFrom":subQ1}),-1.0]])]});}
            var Q3;
            {var subQ0=sQuery(id+"F17.wireOp",EDGE,"E236");var subQ1=makeQuery(id+"F12.opExtrude","CAP_EDGE",EDGE,{"disambiguationData":[OSD([sQuery(id+"F3.wireOp",EDGE,"E230")])],"isStart":false});var subQ2=makeQuery(id+"F17.imprint","INTERSECT",VERTEX,{"disambiguationData":[OD(0.0)],"derivedFrom":[subQ1,subQ0]});Q3=makeQuery(id+"F17.imprint","IMPRINT",FACE,{"disambiguationData":[TD([[makeQuery(id+"F17.imprint","IMPRINT",EDGE,{"disambiguationData":[TD([[subQ2,-1.0]])],"derivedFrom":subQ0}),-1.0]])]});}
            var Q4;
            {var subQ0=sQuery(id+"F17.wireOp",EDGE,"E248");var subQ1=sQuery(id+"F17.wireOp",EDGE,"E237");var subQ2=makeQuery(id+"F17.imprint","INTERSECT",VERTEX,{"derivedFrom":[subQ1,subQ0]});Q4=makeQuery(id+"F17.imprint","IMPRINT",FACE,{"disambiguationData":[TD([[makeQuery(id+"F17.imprint","IMPRINT",EDGE,{"disambiguationData":[TD([[subQ2,-1.0]])],"derivedFrom":subQ1}),-1.0]])]});}
            var Q5;
            {var subQ0=sQuery(id+"F17.wireOp",EDGE,"E246");var subQ1=sQuery(id+"F17.wireOp",EDGE,"E236");var subQ2=makeQuery(id+"F17.imprint","INTERSECT",VERTEX,{"derivedFrom":[subQ1,subQ0]});Q5=makeQuery(id+"F17.imprint","IMPRINT",FACE,{"disambiguationData":[TD([[makeQuery(id+"F17.imprint","IMPRINT",EDGE,{"disambiguationData":[TD([[subQ2,-1.0]])],"derivedFrom":subQ1}),-1.0]])]});}
            var Q6;
            {var subQ0=sQuery(id+"F17.wireOp",EDGE,"E246");var subQ1=sQuery(id+"F17.wireOp",EDGE,"E237");var subQ2=makeQuery(id+"F17.imprint","INTERSECT",VERTEX,{"derivedFrom":[subQ1,subQ0]});Q6=makeQuery(id+"F17.imprint","IMPRINT",FACE,{"disambiguationData":[TD([[makeQuery(id+"F17.imprint","IMPRINT",EDGE,{"disambiguationData":[TD([[subQ2,-1.0]])],"derivedFrom":subQ1}),-1.0]])]});}
            var Q7;
            {var subQ0=sQuery(id+"F17.wireOp",EDGE,"E246");var subQ1=sQuery(id+"F17.wireOp",EDGE,"E236");var subQ2=makeQuery(id+"F17.imprint","INTERSECT",VERTEX,{"derivedFrom":[subQ1,subQ0]});Q7=makeQuery(id+"F17.imprint","IMPRINT",FACE,{"disambiguationData":[TD([[makeQuery(id+"F17.imprint","IMPRINT",EDGE,{"disambiguationData":[TD([[subQ2,-1.0]])],"derivedFrom":subQ1}),1.0]])]});}
            var Q8;
            {var subQ3=sQuery(id+"F17.wireOp",EDGE,"E245");var subQ5=sQuery(id+"F17.wireOp",EDGE,"E237");var subQ6=makeQuery(id+"F17.imprint","INTERSECT",VERTEX,{"derivedFrom":[subQ5,subQ3]});Q8=makeQuery(id+"F17.imprint","IMPRINT",FACE,{"disambiguationData":[TD([[makeQuery(id+"F17.imprint","IMPRINT",EDGE,{"disambiguationData":[TD([[subQ6,-1.0]])],"derivedFrom":subQ5}),1.0]])]});}
            var Q9;
            {var subQ0=sQuery(id+"F17.wireOp",EDGE,"E240");var subQ1=sQuery(id+"F17.wireOp",EDGE,"E236");var subQ2=makeQuery(id+"F17.imprint","INTERSECT",VERTEX,{"derivedFrom":[subQ1,subQ0]});Q9=makeQuery(id+"F17.imprint","IMPRINT",FACE,{"disambiguationData":[TD([[makeQuery(id+"F17.imprint","IMPRINT",EDGE,{"disambiguationData":[TD([[subQ2,-1.0]])],"derivedFrom":subQ1}),-1.0]])]});}
            var Q10;
            {var subQ0=sQuery(id+"F17.wireOp",EDGE,"E242");var subQ1=sQuery(id+"F17.wireOp",EDGE,"E236");var subQ2=makeQuery(id+"F17.imprint","INTERSECT",VERTEX,{"derivedFrom":[subQ1,subQ0]});Q10=makeQuery(id+"F17.imprint","IMPRINT",FACE,{"disambiguationData":[TD([[makeQuery(id+"F17.imprint","IMPRINT",EDGE,{"disambiguationData":[TD([[subQ2,-1.0]])],"derivedFrom":subQ1}),-1.0]])]});}
            var Q11;
            {var subQ0=sQuery(id+"F17.wireOp",EDGE,"E236");var subQ1=makeQuery(id+"F12.opExtrude","CAP_EDGE",EDGE,{"disambiguationData":[OSD([sQuery(id+"F3.wireOp",EDGE,"E230")])],"isStart":false});var subQ2=makeQuery(id+"F17.imprint","INTERSECT",VERTEX,{"disambiguationData":[OD(1.0)],"derivedFrom":[subQ1,subQ0]});Q11=makeQuery(id+"F17.imprint","IMPRINT",FACE,{"disambiguationData":[TD([[makeQuery(id+"F17.imprint","IMPRINT",EDGE,{"disambiguationData":[TD([[subQ2,1.0]])],"derivedFrom":subQ0}),-1.0]])]});}
            var Q12;
            {var subQ0=sQuery(id+"F17.wireOp",EDGE,"E243");var subQ1=sQuery(id+"F17.wireOp",EDGE,"E236");var subQ2=makeQuery(id+"F17.imprint","INTERSECT",VERTEX,{"derivedFrom":[subQ1,subQ0]});Q12=makeQuery(id+"F17.imprint","IMPRINT",FACE,{"disambiguationData":[TD([[makeQuery(id+"F17.imprint","IMPRINT",EDGE,{"disambiguationData":[TD([[subQ2,-1.0]])],"derivedFrom":subQ1}),-1.0]])]});}
            var Q13;
            {var subQ0=sQuery(id+"F17.wireOp",EDGE,"E241");var subQ1=sQuery(id+"F17.wireOp",EDGE,"E236");var subQ2=makeQuery(id+"F17.imprint","INTERSECT",VERTEX,{"derivedFrom":[subQ1,subQ0]});Q13=makeQuery(id+"F17.imprint","IMPRINT",FACE,{"disambiguationData":[TD([[makeQuery(id+"F17.imprint","IMPRINT",EDGE,{"disambiguationData":[TD([[subQ2,-1.0]])],"derivedFrom":subQ1}),-1.0]])]});}
            var Q14;
            {var subQ0=sQuery(id+"F17.wireOp",EDGE,"E239");var subQ5=sQuery(id+"F17.wireOp",EDGE,"E237");var subQ6=makeQuery(id+"F17.imprint","INTERSECT",VERTEX,{"derivedFrom":[subQ5,subQ0]});Q14=makeQuery(id+"F17.imprint","IMPRINT",FACE,{"disambiguationData":[TD([[makeQuery(id+"F17.imprint","IMPRINT",EDGE,{"disambiguationData":[TD([[subQ6,-1.0]])],"derivedFrom":subQ5}),1.0]])]});}
            var Q15;
            {var subQ0=sQuery(id+"F17.wireOp",EDGE,"E238");Q15=makeQuery(id+"F17.imprint","IMPRINT",FACE,{"disambiguationData":[TD([[makeQuery(id+"F17.imprint","IMPRINT",EDGE,{"derivedFrom":subQ0}),-1.0]])]});}
            var Q16;
            {var subQ0=sQuery(id+"F17.wireOp",EDGE,"E239");var subQ1=sQuery(id+"F17.wireOp",EDGE,"E237");var subQ2=makeQuery(id+"F17.imprint","INTERSECT",VERTEX,{"derivedFrom":[subQ1,subQ0]});Q16=makeQuery(id+"F17.imprint","IMPRINT",FACE,{"disambiguationData":[TD([[makeQuery(id+"F17.imprint","IMPRINT",EDGE,{"disambiguationData":[TD([[subQ2,-1.0]])],"derivedFrom":subQ1}),-1.0]])]});}
            var Q17;
            {var subQ0=sQuery(id+"F17.wireOp",EDGE,"E241");var subQ1=sQuery(id+"F17.wireOp",EDGE,"E237");var subQ2=makeQuery(id+"F17.imprint","INTERSECT",VERTEX,{"derivedFrom":[subQ1,subQ0]});Q17=makeQuery(id+"F17.imprint","IMPRINT",FACE,{"disambiguationData":[TD([[makeQuery(id+"F17.imprint","IMPRINT",EDGE,{"disambiguationData":[TD([[subQ2,-1.0]])],"derivedFrom":subQ1}),-1.0]])]});}
            var Q18;
            {var subQ0=sQuery(id+"F17.wireOp",EDGE,"E241");var subQ1=sQuery(id+"F17.wireOp",EDGE,"E236");var subQ2=makeQuery(id+"F17.imprint","INTERSECT",VERTEX,{"derivedFrom":[subQ1,subQ0]});Q18=makeQuery(id+"F17.imprint","IMPRINT",FACE,{"disambiguationData":[TD([[makeQuery(id+"F17.imprint","IMPRINT",EDGE,{"disambiguationData":[TD([[subQ2,-1.0]])],"derivedFrom":subQ1}),1.0]])]});}
            var Q19;
            {var subQ0=sQuery(id+"F17.wireOp",EDGE,"E243");var subQ1=sQuery(id+"F17.wireOp",EDGE,"E236");var subQ2=makeQuery(id+"F17.imprint","INTERSECT",VERTEX,{"derivedFrom":[subQ1,subQ0]});Q19=makeQuery(id+"F17.imprint","IMPRINT",FACE,{"disambiguationData":[TD([[makeQuery(id+"F17.imprint","IMPRINT",EDGE,{"disambiguationData":[TD([[subQ2,-1.0]])],"derivedFrom":subQ1}),1.0]])]});}
            var Q20;
            {var subQ0=sQuery(id+"F17.wireOp",EDGE,"E243");var subQ1=sQuery(id+"F17.wireOp",EDGE,"E237");var subQ2=makeQuery(id+"F17.imprint","INTERSECT",VERTEX,{"derivedFrom":[subQ1,subQ0]});Q20=makeQuery(id+"F17.imprint","IMPRINT",FACE,{"disambiguationData":[TD([[makeQuery(id+"F17.imprint","IMPRINT",EDGE,{"disambiguationData":[TD([[subQ2,-1.0]])],"derivedFrom":subQ1}),-1.0]])]});}
            extrude(context, id + "F18", {"entities" : qUnion([Q0, Q1, Q2, Q3, Q4, Q5, Q6, Q7, Q8, Q9, Q10, Q11, Q12, Q13, Q14, Q15, Q16, Q17, Q18, Q19, Q20]), "operationType" : NewBodyOperationType.REMOVE, "oppositeDirection" : true, "depth" : 2.54 * mm, "offsetDistance" : 25.4 * mm});
        }
        {
            var Q0;
            {var subQ0=sQuery(id+"F3.wireOp",EDGE,"E230");var subQ2=makeQuery(id+"F12.opExtrude","CAP_EDGE",EDGE,{"disambiguationData":[OSD([subQ0])],"isStart":false});var subQ3=sQuery(id+"F17.wireOp",EDGE,"E237");Q0=makeQuery(id+"F18.boolean.opBoolean","COPY",FACE,{"disambiguationData":[TD([makeQuery(id+"F12.opExtrude","SWEPT_FACE",FACE,{"disambiguationData":[OSD([subQ0])]})])],"derivedFrom":makeQuery(id+"F18.opExtrude","SWEPT_FACE",FACE,{"disambiguationData":[OSD([subQ3]),TDD([makeQuery(id+"F17.imprint","IMPRINT",EDGE,{"disambiguationData":[TD([[makeQuery(id+"F17.imprint","INTERSECT",VERTEX,{"disambiguationData":[OD(0.0)],"derivedFrom":[subQ2,subQ3]}),-1.0]])],"derivedFrom":subQ3})])]})});}
            var Q1;
            {var subQ0=sQuery(id+"F3.wireOp",EDGE,"E230");var subQ3=sQuery(id+"F17.wireOp",EDGE,"E237");var subQ5=sQuery(id+"F17.wireOp",EDGE,"E247");var subQ6=makeQuery(id+"F17.imprint","INTERSECT",VERTEX,{"derivedFrom":[subQ3,subQ5]});Q1=makeQuery(id+"F18.boolean.opBoolean","COPY",FACE,{"disambiguationData":[TD([makeQuery(id+"F12.opExtrude","CAP_FACE",FACE,{"disambiguationData":[OSD([subQ0])],"isStart":true})])],"derivedFrom":makeQuery(id+"F18.opExtrude","SWEPT_FACE",FACE,{"disambiguationData":[OSD([subQ3]),TDD([makeQuery(id+"F17.imprint","IMPRINT",EDGE,{"disambiguationData":[TD([[subQ6,-1.0]])],"derivedFrom":subQ3})])]})});}
            var Q2;
            {var subQ0=sQuery(id+"F3.wireOp",EDGE,"E230");var subQ1=sQuery(id+"F17.wireOp",EDGE,"E245");var subQ2=sQuery(id+"F17.wireOp",EDGE,"E237");var subQ3=makeQuery(id+"F17.imprint","INTERSECT",VERTEX,{"derivedFrom":[subQ2,subQ1]});Q2=makeQuery(id+"F18.boolean.opBoolean","COPY",FACE,{"disambiguationData":[TD([makeQuery(id+"F12.opExtrude","CAP_FACE",FACE,{"disambiguationData":[OSD([subQ0])],"isStart":true})])],"derivedFrom":makeQuery(id+"F18.opExtrude","SWEPT_FACE",FACE,{"disambiguationData":[OSD([subQ2]),TDD([makeQuery(id+"F17.imprint","IMPRINT",EDGE,{"disambiguationData":[TD([[subQ3,-1.0]])],"derivedFrom":subQ2})])]})});}
            var Q3;
            {var subQ0=sQuery(id+"F3.wireOp",EDGE,"E230");var subQ1=sQuery(id+"F17.wireOp",EDGE,"E240");var subQ3=sQuery(id+"F17.wireOp",EDGE,"E237");var subQ4=makeQuery(id+"F17.imprint","INTERSECT",VERTEX,{"derivedFrom":[subQ3,subQ1]});Q3=makeQuery(id+"F18.boolean.opBoolean","COPY",FACE,{"disambiguationData":[TD([makeQuery(id+"F12.opExtrude","CAP_FACE",FACE,{"disambiguationData":[OSD([subQ0])],"isStart":true})])],"derivedFrom":makeQuery(id+"F18.opExtrude","SWEPT_FACE",FACE,{"disambiguationData":[OSD([subQ3]),TDD([makeQuery(id+"F17.imprint","IMPRINT",EDGE,{"disambiguationData":[TD([[subQ4,-1.0]])],"derivedFrom":subQ3})])]})});}
            var Q4;
            {var subQ0=sQuery(id+"F3.wireOp",EDGE,"E230");var subQ3=sQuery(id+"F17.wireOp",EDGE,"E237");var subQ5=sQuery(id+"F17.wireOp",EDGE,"E242");var subQ6=makeQuery(id+"F17.imprint","INTERSECT",VERTEX,{"derivedFrom":[subQ3,subQ5]});Q4=makeQuery(id+"F18.boolean.opBoolean","COPY",FACE,{"disambiguationData":[TD([makeQuery(id+"F12.opExtrude","CAP_FACE",FACE,{"disambiguationData":[OSD([subQ0])],"isStart":true})])],"derivedFrom":makeQuery(id+"F18.opExtrude","SWEPT_FACE",FACE,{"disambiguationData":[OSD([subQ3]),TDD([makeQuery(id+"F17.imprint","IMPRINT",EDGE,{"disambiguationData":[TD([[subQ6,-1.0]])],"derivedFrom":subQ3})])]})});}
            var Q5;
            {var subQ0=sQuery(id+"F3.wireOp",EDGE,"E230");var subQ2=makeQuery(id+"F12.opExtrude","CAP_EDGE",EDGE,{"disambiguationData":[OSD([subQ0])],"isStart":false});var subQ3=sQuery(id+"F17.wireOp",EDGE,"E237");Q5=makeQuery(id+"F18.boolean.opBoolean","COPY",FACE,{"disambiguationData":[TD([makeQuery(id+"F12.opExtrude","SWEPT_FACE",FACE,{"disambiguationData":[OSD([subQ0])]})])],"derivedFrom":makeQuery(id+"F18.opExtrude","SWEPT_FACE",FACE,{"disambiguationData":[OSD([subQ3]),TDD([makeQuery(id+"F17.imprint","IMPRINT",EDGE,{"disambiguationData":[TD([[makeQuery(id+"F17.imprint","INTERSECT",VERTEX,{"disambiguationData":[OD(1.0)],"derivedFrom":[subQ2,subQ3]}),1.0]])],"derivedFrom":subQ3})])]})});}
            var Q6;
            {var subQ0=sQuery(id+"F3.wireOp",EDGE,"E230");var subQ2=makeQuery(id+"F12.opExtrude","CAP_EDGE",EDGE,{"disambiguationData":[OSD([subQ0])],"isStart":false});var subQ3=sQuery(id+"F17.wireOp",EDGE,"E236");Q6=makeQuery(id+"F18.boolean.opBoolean","COPY",FACE,{"disambiguationData":[TD([makeQuery(id+"F12.opExtrude","SWEPT_FACE",FACE,{"disambiguationData":[OSD([subQ0])]})])],"derivedFrom":makeQuery(id+"F18.opExtrude","SWEPT_FACE",FACE,{"disambiguationData":[OSD([subQ3]),TDD([makeQuery(id+"F17.imprint","IMPRINT",EDGE,{"disambiguationData":[TD([[makeQuery(id+"F17.imprint","INTERSECT",VERTEX,{"disambiguationData":[OD(1.0)],"derivedFrom":[subQ2,subQ3]}),1.0]])],"derivedFrom":subQ3})])]})});}
            var Q7;
            {var subQ0=sQuery(id+"F3.wireOp",EDGE,"E230");var subQ3=sQuery(id+"F17.wireOp",EDGE,"E236");var subQ5=sQuery(id+"F17.wireOp",EDGE,"E242");var subQ6=makeQuery(id+"F17.imprint","INTERSECT",VERTEX,{"derivedFrom":[subQ3,subQ5]});Q7=makeQuery(id+"F18.boolean.opBoolean","COPY",FACE,{"disambiguationData":[TD([makeQuery(id+"F12.opExtrude","CAP_FACE",FACE,{"disambiguationData":[OSD([subQ0])],"isStart":true})])],"derivedFrom":makeQuery(id+"F18.opExtrude","SWEPT_FACE",FACE,{"disambiguationData":[OSD([subQ3]),TDD([makeQuery(id+"F17.imprint","IMPRINT",EDGE,{"disambiguationData":[TD([[subQ6,-1.0]])],"derivedFrom":subQ3})])]})});}
            var Q8;
            {var subQ0=sQuery(id+"F3.wireOp",EDGE,"E230");var subQ1=sQuery(id+"F17.wireOp",EDGE,"E240");var subQ3=sQuery(id+"F17.wireOp",EDGE,"E236");var subQ4=makeQuery(id+"F17.imprint","INTERSECT",VERTEX,{"derivedFrom":[subQ3,subQ1]});Q8=makeQuery(id+"F18.boolean.opBoolean","COPY",FACE,{"disambiguationData":[TD([makeQuery(id+"F12.opExtrude","CAP_FACE",FACE,{"disambiguationData":[OSD([subQ0])],"isStart":true})])],"derivedFrom":makeQuery(id+"F18.opExtrude","SWEPT_FACE",FACE,{"disambiguationData":[OSD([subQ3]),TDD([makeQuery(id+"F17.imprint","IMPRINT",EDGE,{"disambiguationData":[TD([[subQ4,-1.0]])],"derivedFrom":subQ3})])]})});}
            var Q9;
            {var subQ0=sQuery(id+"F3.wireOp",EDGE,"E230");var subQ2=sQuery(id+"F17.wireOp",EDGE,"E245");var subQ3=sQuery(id+"F17.wireOp",EDGE,"E236");var subQ4=makeQuery(id+"F17.imprint","INTERSECT",VERTEX,{"derivedFrom":[subQ3,subQ2]});Q9=makeQuery(id+"F18.boolean.opBoolean","COPY",FACE,{"disambiguationData":[TD([makeQuery(id+"F12.opExtrude","CAP_FACE",FACE,{"disambiguationData":[OSD([subQ0])],"isStart":true})])],"derivedFrom":makeQuery(id+"F18.opExtrude","SWEPT_FACE",FACE,{"disambiguationData":[OSD([subQ3]),TDD([makeQuery(id+"F17.imprint","IMPRINT",EDGE,{"disambiguationData":[TD([[subQ4,-1.0]])],"derivedFrom":subQ3})])]})});}
            var Q10;
            {var subQ0=sQuery(id+"F3.wireOp",EDGE,"E230");var subQ3=sQuery(id+"F17.wireOp",EDGE,"E236");var subQ5=sQuery(id+"F17.wireOp",EDGE,"E247");var subQ6=makeQuery(id+"F17.imprint","INTERSECT",VERTEX,{"derivedFrom":[subQ3,subQ5]});Q10=makeQuery(id+"F18.boolean.opBoolean","COPY",FACE,{"disambiguationData":[TD([makeQuery(id+"F12.opExtrude","CAP_FACE",FACE,{"disambiguationData":[OSD([subQ0])],"isStart":true})])],"derivedFrom":makeQuery(id+"F18.opExtrude","SWEPT_FACE",FACE,{"disambiguationData":[OSD([subQ3]),TDD([makeQuery(id+"F17.imprint","IMPRINT",EDGE,{"disambiguationData":[TD([[subQ6,-1.0]])],"derivedFrom":subQ3})])]})});}
            var Q11;
            {var subQ0=sQuery(id+"F3.wireOp",EDGE,"E230");var subQ2=makeQuery(id+"F12.opExtrude","CAP_EDGE",EDGE,{"disambiguationData":[OSD([subQ0])],"isStart":false});var subQ3=sQuery(id+"F17.wireOp",EDGE,"E236");Q11=makeQuery(id+"F18.boolean.opBoolean","COPY",FACE,{"disambiguationData":[TD([makeQuery(id+"F12.opExtrude","SWEPT_FACE",FACE,{"disambiguationData":[OSD([subQ0])]})])],"derivedFrom":makeQuery(id+"F18.opExtrude","SWEPT_FACE",FACE,{"disambiguationData":[OSD([subQ3]),TDD([makeQuery(id+"F17.imprint","IMPRINT",EDGE,{"disambiguationData":[TD([[makeQuery(id+"F17.imprint","INTERSECT",VERTEX,{"disambiguationData":[OD(0.0)],"derivedFrom":[subQ2,subQ3]}),-1.0]])],"derivedFrom":subQ3})])]})});}
            var Q12;
            {var subQ0=sQuery(id+"F3.wireOp",EDGE,"E230");var subQ2=makeQuery(id+"F12.opExtrude","CAP_EDGE",EDGE,{"disambiguationData":[OSD([subQ0])],"isStart":false});var subQ3=sQuery(id+"F17.wireOp",EDGE,"E248");Q12=makeQuery(id+"F18.boolean.opBoolean","COPY",FACE,{"disambiguationData":[TD([makeQuery(id+"F12.opExtrude","SWEPT_FACE",FACE,{"disambiguationData":[OSD([subQ0])]})])],"derivedFrom":makeQuery(id+"F18.opExtrude","SWEPT_FACE",FACE,{"disambiguationData":[OSD([subQ3]),TDD([makeQuery(id+"F17.imprint","IMPRINT",EDGE,{"disambiguationData":[TD([[makeQuery(id+"F17.imprint","INTERSECT",VERTEX,{"disambiguationData":[OD(0.0)],"derivedFrom":[subQ2,subQ3]}),-1.0]])],"derivedFrom":subQ3})])]})});}
            var Q13;
            {var subQ0=sQuery(id+"F3.wireOp",EDGE,"E230");var subQ2=sQuery(id+"F17.wireOp",EDGE,"E246");Q13=makeQuery(id+"F18.boolean.opBoolean","COPY",FACE,{"disambiguationData":[TD([makeQuery(id+"F12.opExtrude","SWEPT_FACE",FACE,{"disambiguationData":[OSD([subQ0])]})])],"derivedFrom":makeQuery(id+"F18.opExtrude","SWEPT_FACE",FACE,{"disambiguationData":[OSD([subQ2]),TDD([makeQuery(id+"F17.imprint","IMPRINT",EDGE,{"disambiguationData":[TD([[makeQuery(id+"F17.imprint","INTERSECT",VERTEX,{"disambiguationData":[OD(0.0)],"derivedFrom":[makeQuery(id+"F12.opExtrude","CAP_EDGE",EDGE,{"disambiguationData":[OSD([subQ0])],"isStart":false}),subQ2]}),-1.0]])],"derivedFrom":subQ2})])]})});}
            var Q14;
            {var subQ0=sQuery(id+"F3.wireOp",EDGE,"E230");var subQ1=sQuery(id+"F17.wireOp",EDGE,"E238");Q14=makeQuery(id+"F18.boolean.opBoolean","COPY",FACE,{"disambiguationData":[TD([makeQuery(id+"F12.opExtrude","SWEPT_FACE",FACE,{"disambiguationData":[OSD([subQ0])]})])],"derivedFrom":makeQuery(id+"F18.opExtrude","SWEPT_FACE",FACE,{"disambiguationData":[OSD([subQ1])]})});}
            var Q15;
            {var subQ0=sQuery(id+"F3.wireOp",EDGE,"E230");var subQ2=sQuery(id+"F17.wireOp",EDGE,"E241");Q15=makeQuery(id+"F18.boolean.opBoolean","COPY",FACE,{"disambiguationData":[TD([makeQuery(id+"F12.opExtrude","SWEPT_FACE",FACE,{"disambiguationData":[OSD([subQ0])]})])],"derivedFrom":makeQuery(id+"F18.opExtrude","SWEPT_FACE",FACE,{"disambiguationData":[OSD([subQ2]),TDD([makeQuery(id+"F17.imprint","IMPRINT",EDGE,{"disambiguationData":[TD([[makeQuery(id+"F17.imprint","INTERSECT",VERTEX,{"disambiguationData":[OD(0.0)],"derivedFrom":[makeQuery(id+"F12.opExtrude","CAP_EDGE",EDGE,{"disambiguationData":[OSD([subQ0])],"isStart":false}),subQ2]}),-1.0]])],"derivedFrom":subQ2})])]})});}
            var Q16;
            {var subQ0=sQuery(id+"F3.wireOp",EDGE,"E230");var subQ2=sQuery(id+"F17.wireOp",EDGE,"E243");Q16=makeQuery(id+"F18.boolean.opBoolean","COPY",FACE,{"disambiguationData":[TD([makeQuery(id+"F12.opExtrude","SWEPT_FACE",FACE,{"disambiguationData":[OSD([subQ0])]})])],"derivedFrom":makeQuery(id+"F18.opExtrude","SWEPT_FACE",FACE,{"disambiguationData":[OSD([subQ2]),TDD([makeQuery(id+"F17.imprint","IMPRINT",EDGE,{"disambiguationData":[TD([[makeQuery(id+"F17.imprint","INTERSECT",VERTEX,{"disambiguationData":[OD(0.0)],"derivedFrom":[makeQuery(id+"F12.opExtrude","CAP_EDGE",EDGE,{"disambiguationData":[OSD([subQ0])],"isStart":false}),subQ2]}),-1.0]])],"derivedFrom":subQ2})])]})});}
            var Q17;
            {var subQ0=sQuery(id+"F3.wireOp",EDGE,"E230");var subQ2=sQuery(id+"F17.wireOp",EDGE,"E243");Q17=makeQuery(id+"F18.boolean.opBoolean","COPY",FACE,{"disambiguationData":[TD([makeQuery(id+"F12.opExtrude","SWEPT_FACE",FACE,{"disambiguationData":[OSD([subQ0])]})])],"derivedFrom":makeQuery(id+"F18.opExtrude","SWEPT_FACE",FACE,{"disambiguationData":[OSD([subQ2]),TDD([makeQuery(id+"F17.imprint","IMPRINT",EDGE,{"disambiguationData":[TD([[makeQuery(id+"F17.imprint","INTERSECT",VERTEX,{"disambiguationData":[OD(1.0)],"derivedFrom":[makeQuery(id+"F12.opExtrude","CAP_EDGE",EDGE,{"disambiguationData":[OSD([subQ0])],"isStart":false}),subQ2]}),1.0]])],"derivedFrom":subQ2})])]})});}
            var Q18;
            {var subQ0=sQuery(id+"F3.wireOp",EDGE,"E230");var subQ2=sQuery(id+"F17.wireOp",EDGE,"E241");Q18=makeQuery(id+"F18.boolean.opBoolean","COPY",FACE,{"disambiguationData":[TD([makeQuery(id+"F12.opExtrude","SWEPT_FACE",FACE,{"disambiguationData":[OSD([subQ0])]})])],"derivedFrom":makeQuery(id+"F18.opExtrude","SWEPT_FACE",FACE,{"disambiguationData":[OSD([subQ2]),TDD([makeQuery(id+"F17.imprint","IMPRINT",EDGE,{"disambiguationData":[TD([[makeQuery(id+"F17.imprint","INTERSECT",VERTEX,{"disambiguationData":[OD(1.0)],"derivedFrom":[makeQuery(id+"F12.opExtrude","CAP_EDGE",EDGE,{"disambiguationData":[OSD([subQ0])],"isStart":false}),subQ2]}),1.0]])],"derivedFrom":subQ2})])]})});}
            var Q19;
            {var subQ0=sQuery(id+"F3.wireOp",EDGE,"E230");var subQ2=sQuery(id+"F17.wireOp",EDGE,"E239");Q19=makeQuery(id+"F18.boolean.opBoolean","COPY",FACE,{"disambiguationData":[TD([makeQuery(id+"F12.opExtrude","SWEPT_FACE",FACE,{"disambiguationData":[OSD([subQ0])]})])],"derivedFrom":makeQuery(id+"F18.opExtrude","SWEPT_FACE",FACE,{"disambiguationData":[OSD([subQ2])]})});}
            var Q20;
            {var subQ0=sQuery(id+"F3.wireOp",EDGE,"E230");var subQ2=sQuery(id+"F17.wireOp",EDGE,"E246");Q20=makeQuery(id+"F18.boolean.opBoolean","COPY",FACE,{"disambiguationData":[TD([makeQuery(id+"F12.opExtrude","SWEPT_FACE",FACE,{"disambiguationData":[OSD([subQ0])]})])],"derivedFrom":makeQuery(id+"F18.opExtrude","SWEPT_FACE",FACE,{"disambiguationData":[OSD([subQ2]),TDD([makeQuery(id+"F17.imprint","IMPRINT",EDGE,{"disambiguationData":[TD([[makeQuery(id+"F17.imprint","INTERSECT",VERTEX,{"disambiguationData":[OD(1.0)],"derivedFrom":[makeQuery(id+"F12.opExtrude","CAP_EDGE",EDGE,{"disambiguationData":[OSD([subQ0])],"isStart":false}),subQ2]}),1.0]])],"derivedFrom":subQ2})])]})});}
            var Q21;
            {var subQ0=sQuery(id+"F3.wireOp",EDGE,"E230");var subQ2=makeQuery(id+"F12.opExtrude","CAP_EDGE",EDGE,{"disambiguationData":[OSD([subQ0])],"isStart":false});var subQ3=sQuery(id+"F17.wireOp",EDGE,"E248");Q21=makeQuery(id+"F18.boolean.opBoolean","COPY",FACE,{"disambiguationData":[TD([makeQuery(id+"F12.opExtrude","SWEPT_FACE",FACE,{"disambiguationData":[OSD([subQ0])]})])],"derivedFrom":makeQuery(id+"F18.opExtrude","SWEPT_FACE",FACE,{"disambiguationData":[OSD([subQ3]),TDD([makeQuery(id+"F17.imprint","IMPRINT",EDGE,{"disambiguationData":[TD([[makeQuery(id+"F17.imprint","INTERSECT",VERTEX,{"disambiguationData":[OD(1.0)],"derivedFrom":[subQ2,subQ3]}),1.0]])],"derivedFrom":subQ3})])]})});}
            var Q22;
            {var subQ0=sQuery(id+"F3.wireOp",EDGE,"E230");var subQ1=sQuery(id+"F17.wireOp",EDGE,"E247");Q22=makeQuery(id+"F18.boolean.opBoolean","COPY",FACE,{"disambiguationData":[TD([makeQuery(id+"F12.opExtrude","SWEPT_FACE",FACE,{"disambiguationData":[OSD([subQ0])]})])],"derivedFrom":makeQuery(id+"F18.opExtrude","SWEPT_FACE",FACE,{"disambiguationData":[OSD([subQ1]),TDD([makeQuery(id+"F17.imprint","IMPRINT",EDGE,{"disambiguationData":[TD([[makeQuery(id+"F17.imprint","INTERSECT",VERTEX,{"disambiguationData":[OD(0.0)],"derivedFrom":[makeQuery(id+"F12.opExtrude","CAP_EDGE",EDGE,{"disambiguationData":[OSD([subQ0])],"isStart":false}),subQ1]}),-1.0]])],"derivedFrom":subQ1})])]})});}
            var Q23;
            {var subQ0=sQuery(id+"F3.wireOp",EDGE,"E230");var subQ2=sQuery(id+"F17.wireOp",EDGE,"E245");Q23=makeQuery(id+"F18.boolean.opBoolean","COPY",FACE,{"disambiguationData":[TD([makeQuery(id+"F12.opExtrude","SWEPT_FACE",FACE,{"disambiguationData":[OSD([subQ0])]})])],"derivedFrom":makeQuery(id+"F18.opExtrude","SWEPT_FACE",FACE,{"disambiguationData":[OSD([subQ2]),TDD([makeQuery(id+"F17.imprint","IMPRINT",EDGE,{"disambiguationData":[TD([[makeQuery(id+"F17.imprint","INTERSECT",VERTEX,{"disambiguationData":[OD(0.0)],"derivedFrom":[makeQuery(id+"F12.opExtrude","CAP_EDGE",EDGE,{"disambiguationData":[OSD([subQ0])],"isStart":false}),subQ2]}),-1.0]])],"derivedFrom":subQ2})])]})});}
            var Q24;
            {var subQ0=sQuery(id+"F3.wireOp",EDGE,"E230");var subQ1=sQuery(id+"F17.wireOp",EDGE,"E240");Q24=makeQuery(id+"F18.boolean.opBoolean","COPY",FACE,{"disambiguationData":[TD([makeQuery(id+"F12.opExtrude","SWEPT_FACE",FACE,{"disambiguationData":[OSD([subQ0])]})])],"derivedFrom":makeQuery(id+"F18.opExtrude","SWEPT_FACE",FACE,{"disambiguationData":[OSD([subQ1]),TDD([makeQuery(id+"F17.imprint","IMPRINT",EDGE,{"disambiguationData":[TD([[makeQuery(id+"F17.imprint","INTERSECT",VERTEX,{"disambiguationData":[OD(1.0)],"derivedFrom":[makeQuery(id+"F12.opExtrude","CAP_EDGE",EDGE,{"disambiguationData":[OSD([subQ0])],"isStart":false}),subQ1]}),1.0]])],"derivedFrom":subQ1})])]})});}
            var Q25;
            {var subQ0=sQuery(id+"F3.wireOp",EDGE,"E230");var subQ1=sQuery(id+"F17.wireOp",EDGE,"E242");Q25=makeQuery(id+"F18.boolean.opBoolean","COPY",FACE,{"disambiguationData":[TD([makeQuery(id+"F12.opExtrude","SWEPT_FACE",FACE,{"disambiguationData":[OSD([subQ0])]})])],"derivedFrom":makeQuery(id+"F18.opExtrude","SWEPT_FACE",FACE,{"disambiguationData":[OSD([subQ1]),TDD([makeQuery(id+"F17.imprint","IMPRINT",EDGE,{"disambiguationData":[TD([[makeQuery(id+"F17.imprint","INTERSECT",VERTEX,{"disambiguationData":[OD(1.0)],"derivedFrom":[makeQuery(id+"F12.opExtrude","CAP_EDGE",EDGE,{"disambiguationData":[OSD([subQ0])],"isStart":false}),subQ1]}),1.0]])],"derivedFrom":subQ1})])]})});}
            var Q26;
            {var subQ0=sQuery(id+"F3.wireOp",EDGE,"E230");var subQ2=makeQuery(id+"F12.opExtrude","CAP_EDGE",EDGE,{"disambiguationData":[OSD([subQ0])],"isStart":false});var subQ3=sQuery(id+"F17.wireOp",EDGE,"E244");Q26=makeQuery(id+"F18.boolean.opBoolean","COPY",FACE,{"disambiguationData":[TD([makeQuery(id+"F12.opExtrude","SWEPT_FACE",FACE,{"disambiguationData":[OSD([subQ0])]})])],"derivedFrom":makeQuery(id+"F18.opExtrude","SWEPT_FACE",FACE,{"disambiguationData":[OSD([subQ3]),TDD([makeQuery(id+"F17.imprint","IMPRINT",EDGE,{"disambiguationData":[TD([[makeQuery(id+"F17.imprint","INTERSECT",VERTEX,{"disambiguationData":[OD(1.0)],"derivedFrom":[subQ2,subQ3]}),1.0]])],"derivedFrom":subQ3})])]})});}
            var Q27;
            {var subQ0=sQuery(id+"F3.wireOp",EDGE,"E230");var subQ2=makeQuery(id+"F12.opExtrude","CAP_EDGE",EDGE,{"disambiguationData":[OSD([subQ0])],"isStart":false});var subQ3=sQuery(id+"F17.wireOp",EDGE,"E244");Q27=makeQuery(id+"F18.boolean.opBoolean","COPY",FACE,{"disambiguationData":[TD([makeQuery(id+"F12.opExtrude","SWEPT_FACE",FACE,{"disambiguationData":[OSD([subQ0])]})])],"derivedFrom":makeQuery(id+"F18.opExtrude","SWEPT_FACE",FACE,{"disambiguationData":[OSD([subQ3]),TDD([makeQuery(id+"F17.imprint","IMPRINT",EDGE,{"disambiguationData":[TD([[makeQuery(id+"F17.imprint","INTERSECT",VERTEX,{"disambiguationData":[OD(0.0)],"derivedFrom":[subQ2,subQ3]}),-1.0]])],"derivedFrom":subQ3})])]})});}
            var Q28;
            {var subQ0=sQuery(id+"F3.wireOp",EDGE,"E230");var subQ1=sQuery(id+"F17.wireOp",EDGE,"E242");Q28=makeQuery(id+"F18.boolean.opBoolean","COPY",FACE,{"disambiguationData":[TD([makeQuery(id+"F12.opExtrude","SWEPT_FACE",FACE,{"disambiguationData":[OSD([subQ0])]})])],"derivedFrom":makeQuery(id+"F18.opExtrude","SWEPT_FACE",FACE,{"disambiguationData":[OSD([subQ1]),TDD([makeQuery(id+"F17.imprint","IMPRINT",EDGE,{"disambiguationData":[TD([[makeQuery(id+"F17.imprint","INTERSECT",VERTEX,{"disambiguationData":[OD(0.0)],"derivedFrom":[makeQuery(id+"F12.opExtrude","CAP_EDGE",EDGE,{"disambiguationData":[OSD([subQ0])],"isStart":false}),subQ1]}),-1.0]])],"derivedFrom":subQ1})])]})});}
            var Q29;
            {var subQ0=sQuery(id+"F3.wireOp",EDGE,"E230");var subQ1=sQuery(id+"F17.wireOp",EDGE,"E240");Q29=makeQuery(id+"F18.boolean.opBoolean","COPY",FACE,{"disambiguationData":[TD([makeQuery(id+"F12.opExtrude","SWEPT_FACE",FACE,{"disambiguationData":[OSD([subQ0])]})])],"derivedFrom":makeQuery(id+"F18.opExtrude","SWEPT_FACE",FACE,{"disambiguationData":[OSD([subQ1]),TDD([makeQuery(id+"F17.imprint","IMPRINT",EDGE,{"disambiguationData":[TD([[makeQuery(id+"F17.imprint","INTERSECT",VERTEX,{"disambiguationData":[OD(0.0)],"derivedFrom":[makeQuery(id+"F12.opExtrude","CAP_EDGE",EDGE,{"disambiguationData":[OSD([subQ0])],"isStart":false}),subQ1]}),-1.0]])],"derivedFrom":subQ1})])]})});}
            var Q30;
            {var subQ0=sQuery(id+"F3.wireOp",EDGE,"E230");var subQ1=sQuery(id+"F17.wireOp",EDGE,"E245");Q30=makeQuery(id+"F18.boolean.opBoolean","COPY",FACE,{"disambiguationData":[TD([makeQuery(id+"F12.opExtrude","SWEPT_FACE",FACE,{"disambiguationData":[OSD([subQ0])]})])],"derivedFrom":makeQuery(id+"F18.opExtrude","SWEPT_FACE",FACE,{"disambiguationData":[OSD([subQ1]),TDD([makeQuery(id+"F17.imprint","IMPRINT",EDGE,{"disambiguationData":[TD([[makeQuery(id+"F17.imprint","INTERSECT",VERTEX,{"disambiguationData":[OD(1.0)],"derivedFrom":[makeQuery(id+"F12.opExtrude","CAP_EDGE",EDGE,{"disambiguationData":[OSD([subQ0])],"isStart":false}),subQ1]}),1.0]])],"derivedFrom":subQ1})])]})});}
            var Q31;
            {var subQ0=sQuery(id+"F3.wireOp",EDGE,"E230");var subQ1=sQuery(id+"F17.wireOp",EDGE,"E247");Q31=makeQuery(id+"F18.boolean.opBoolean","COPY",FACE,{"disambiguationData":[TD([makeQuery(id+"F12.opExtrude","SWEPT_FACE",FACE,{"disambiguationData":[OSD([subQ0])]})])],"derivedFrom":makeQuery(id+"F18.opExtrude","SWEPT_FACE",FACE,{"disambiguationData":[OSD([subQ1]),TDD([makeQuery(id+"F17.imprint","IMPRINT",EDGE,{"disambiguationData":[TD([[makeQuery(id+"F17.imprint","INTERSECT",VERTEX,{"disambiguationData":[OD(1.0)],"derivedFrom":[makeQuery(id+"F12.opExtrude","CAP_EDGE",EDGE,{"disambiguationData":[OSD([subQ0])],"isStart":false}),subQ1]}),1.0]])],"derivedFrom":subQ1})])]})});}
            fillet(context, id + "F19", {"entities" : qUnion([Q0, Q1, Q2, Q3, Q4, Q5, Q6, Q7, Q8, Q9, Q10, Q11, Q12, Q13, Q14, Q15, Q16, Q17, Q18, Q19, Q20, Q21, Q22, Q23, Q24, Q25, Q26, Q27, Q28, Q29, Q30, Q31]), "radius" : 0.76 * mm, "tangentPropagation" : true, "allowEdgeOverflow" : false});
        }
        {
            var Q0;
            {var subQ1=sQuery(id+"F0.wireOp",EDGE,"E5");Q0=makeQuery(id+"F0.imprint","IMPRINT",FACE,{"disambiguationData":[TD([[makeQuery(id+"F0.imprint","IMPRINT",EDGE,{"derivedFrom":subQ1}),1.0]])]});}
            var Q1;
            {var subQ1=sQuery(id+"F0.wireOp",EDGE,"E19");Q1=makeQuery(id+"F0.imprint","IMPRINT",FACE,{"disambiguationData":[TD([[makeQuery(id+"F0.imprint","IMPRINT",EDGE,{"derivedFrom":subQ1}),1.0]])]});}
            var Q2;
            Q2=makeQuery(id+"F0.imprint","IMPRINT",FACE,{"disambiguationData":[TD([[makeQuery(id+"F0.imprint","IMPRINT",EDGE,{"derivedFrom":sQuery(id+"F0.wireOp",EDGE,"3e5dcf01-7677-4fba-a706-698ddb1a2f2c1.MirrorCS")}),1.0]])]});
            var Q3;
            Q3=makeQuery(id+"F0.imprint","IMPRINT",FACE,{"disambiguationData":[TD([[makeQuery(id+"F0.imprint","IMPRINT",EDGE,{"derivedFrom":sQuery(id+"F0.wireOp",EDGE,"E110.MirrorCS")}),-1.0]])]});
            var Q4;
            Q4=makeQuery(id+"F0.imprint","IMPRINT",FACE,{"disambiguationData":[TD([[makeQuery(id+"F0.imprint","IMPRINT",EDGE,{"derivedFrom":sQuery(id+"F0.wireOp",EDGE,"E120.MirrorCS")}),-1.0]])]});
            extrude(context, id + "F20", {"entities" : qUnion([Q0, Q1, Q2, Q3, Q4]), "depth" : 2.03 * mm, "offsetDistance" : 25.4 * mm});
        }
        {
            var Q0;
            {var subQ5=sQuery(id+"F0.wireOp",EDGE,"E19");Q0=makeQuery(id+"F0.imprint","IMPRINT",FACE,{"disambiguationData":[TD([[makeQuery(id+"F0.imprint","IMPRINT",EDGE,{"derivedFrom":subQ5}),-1.0]])]});}
            var Q1;
            {var subQ6=sQuery(id+"F0.wireOp",EDGE,"E5");Q1=makeQuery(id+"F0.imprint","IMPRINT",FACE,{"disambiguationData":[TD([[makeQuery(id+"F0.imprint","IMPRINT",EDGE,{"derivedFrom":subQ6}),-1.0]])]});}
            var Q2;
            Q2=makeQuery(id+"F0.imprint","IMPRINT",FACE,{"disambiguationData":[TD([[makeQuery(id+"F0.imprint","IMPRINT",EDGE,{"derivedFrom":sQuery(id+"F0.wireOp",EDGE,"E41.MirrorCS")}),1.0]])]});
            var Q3;
            Q3=makeQuery(id+"F0.imprint","IMPRINT",FACE,{"disambiguationData":[TD([[makeQuery(id+"F0.imprint","IMPRINT",EDGE,{"derivedFrom":sQuery(id+"F0.wireOp",EDGE,"E30.MirrorCS")}),1.0]])]});
            extrude(context, id + "F21", {"entities" : qUnion([Q0, Q1, Q2, Q3]), "depth" : 3.3 * mm, "offsetDistance" : 25.4 * mm});
        }
        {
            var Q0;
            Q0=makeQuery(id+"F21.opExtrude","CAP_EDGE",EDGE,{"disambiguationData":[OSD([sQuery(id+"F0.wireOp",EDGE,"E15")])],"isStart":false});
            var Q1;
            Q1=makeQuery(id+"F21.opExtrude","CAP_EDGE",EDGE,{"disambiguationData":[OSD([sQuery(id+"F0.wireOp",EDGE,"E14")])],"isStart":false});
            var Q2;
            Q2=makeQuery(id+"F21.opExtrude","CAP_EDGE",EDGE,{"disambiguationData":[OSD([sQuery(id+"F0.wireOp",EDGE,"E5")])],"isStart":false});
            var Q3;
            Q3=makeQuery(id+"F21.opExtrude","CAP_EDGE",EDGE,{"disambiguationData":[OSD([sQuery(id+"F0.wireOp",EDGE,"E6")])],"isStart":false});
            var Q4;
            Q4=makeQuery(id+"F21.opExtrude","CAP_EDGE",EDGE,{"disambiguationData":[OSD([sQuery(id+"F0.wireOp",EDGE,"E13")])],"isStart":false});
            var Q5;
            Q5=makeQuery(id+"F21.opExtrude","CAP_EDGE",EDGE,{"disambiguationData":[OSD([sQuery(id+"F0.wireOp",EDGE,"E12")])],"isStart":false});
            var Q6;
            Q6=makeQuery(id+"F21.opExtrude","CAP_EDGE",EDGE,{"disambiguationData":[OSD([sQuery(id+"F0.wireOp",EDGE,"E7")])],"isStart":false});
            var Q7;
            Q7=makeQuery(id+"F21.opExtrude","CAP_EDGE",EDGE,{"disambiguationData":[OSD([sQuery(id+"F0.wireOp",EDGE,"E11")])],"isStart":false});
            var Q8;
            Q8=makeQuery(id+"F21.opExtrude","CAP_EDGE",EDGE,{"disambiguationData":[OSD([sQuery(id+"F0.wireOp",EDGE,"E8")])],"isStart":false});
            var Q9;
            Q9=makeQuery(id+"F21.opExtrude","CAP_EDGE",EDGE,{"disambiguationData":[OSD([sQuery(id+"F0.wireOp",EDGE,"E10")])],"isStart":false});
            var Q10;
            Q10=makeQuery(id+"F21.opExtrude","CAP_EDGE",EDGE,{"disambiguationData":[OSD([sQuery(id+"F0.wireOp",EDGE,"E9")])],"isStart":false});
            var Q11;
            Q11=makeQuery(id+"F21.opExtrude","CAP_EDGE",EDGE,{"disambiguationData":[OSD([sQuery(id+"F0.wireOp",EDGE,"E4")])],"isStart":true});
            var Q12;
            Q12=makeQuery(id+"F21.opExtrude","CAP_EDGE",EDGE,{"disambiguationData":[OSD([sQuery(id+"F0.wireOp",EDGE,"E15")])],"isStart":true});
            var Q13;
            Q13=makeQuery(id+"F21.opExtrude","CAP_EDGE",EDGE,{"disambiguationData":[OSD([sQuery(id+"F0.wireOp",EDGE,"E14")])],"isStart":true});
            var Q14;
            Q14=makeQuery(id+"F21.opExtrude","CAP_EDGE",EDGE,{"disambiguationData":[OSD([sQuery(id+"F0.wireOp",EDGE,"E5")])],"isStart":true});
            var Q15;
            Q15=makeQuery(id+"F21.opExtrude","CAP_EDGE",EDGE,{"disambiguationData":[OSD([sQuery(id+"F0.wireOp",EDGE,"E13")])],"isStart":true});
            var Q16;
            Q16=makeQuery(id+"F21.opExtrude","CAP_EDGE",EDGE,{"disambiguationData":[OSD([sQuery(id+"F0.wireOp",EDGE,"E6")])],"isStart":true});
            var Q17;
            Q17=makeQuery(id+"F21.opExtrude","CAP_EDGE",EDGE,{"disambiguationData":[OSD([sQuery(id+"F0.wireOp",EDGE,"E12")])],"isStart":true});
            var Q18;
            Q18=makeQuery(id+"F21.opExtrude","CAP_EDGE",EDGE,{"disambiguationData":[OSD([sQuery(id+"F0.wireOp",EDGE,"E7")])],"isStart":true});
            var Q19;
            Q19=makeQuery(id+"F21.opExtrude","CAP_EDGE",EDGE,{"disambiguationData":[OSD([sQuery(id+"F0.wireOp",EDGE,"E8")])],"isStart":true});
            var Q20;
            Q20=makeQuery(id+"F21.opExtrude","CAP_EDGE",EDGE,{"disambiguationData":[OSD([sQuery(id+"F0.wireOp",EDGE,"E11")])],"isStart":true});
            var Q21;
            Q21=makeQuery(id+"F21.opExtrude","CAP_EDGE",EDGE,{"disambiguationData":[OSD([sQuery(id+"F0.wireOp",EDGE,"E10")])],"isStart":true});
            var Q22;
            Q22=makeQuery(id+"F21.opExtrude","CAP_EDGE",EDGE,{"disambiguationData":[OSD([sQuery(id+"F0.wireOp",EDGE,"E9")])],"isStart":true});
            var Q23;
            Q23=makeQuery(id+"F21.opExtrude","CAP_EDGE",EDGE,{"disambiguationData":[OSD([sQuery(id+"F0.wireOp",EDGE,"E29")])],"isStart":false});
            var Q24;
            Q24=makeQuery(id+"F21.opExtrude","CAP_EDGE",EDGE,{"disambiguationData":[OSD([sQuery(id+"F0.wireOp",EDGE,"E28")])],"isStart":false});
            var Q25;
            Q25=makeQuery(id+"F21.opExtrude","CAP_EDGE",EDGE,{"disambiguationData":[OSD([sQuery(id+"F0.wireOp",EDGE,"E27")])],"isStart":false});
            var Q26;
            Q26=makeQuery(id+"F21.opExtrude","CAP_EDGE",EDGE,{"disambiguationData":[OSD([sQuery(id+"F0.wireOp",EDGE,"E26")])],"isStart":false});
            var Q27;
            Q27=makeQuery(id+"F21.opExtrude","CAP_EDGE",EDGE,{"disambiguationData":[OSD([sQuery(id+"F0.wireOp",EDGE,"E25")])],"isStart":false});
            var Q28;
            Q28=makeQuery(id+"F21.opExtrude","CAP_EDGE",EDGE,{"disambiguationData":[OSD([sQuery(id+"F0.wireOp",EDGE,"E24")])],"isStart":false});
            var Q29;
            Q29=makeQuery(id+"F21.opExtrude","CAP_EDGE",EDGE,{"disambiguationData":[OSD([sQuery(id+"F0.wireOp",EDGE,"E18")])],"isStart":false});
            var Q30;
            Q30=makeQuery(id+"F21.opExtrude","CAP_EDGE",EDGE,{"disambiguationData":[OSD([sQuery(id+"F0.wireOp",EDGE,"E19")])],"isStart":false});
            var Q31;
            Q31=makeQuery(id+"F21.opExtrude","CAP_EDGE",EDGE,{"disambiguationData":[OSD([sQuery(id+"F0.wireOp",EDGE,"E20")])],"isStart":false});
            var Q32;
            Q32=makeQuery(id+"F21.opExtrude","CAP_EDGE",EDGE,{"disambiguationData":[OSD([sQuery(id+"F0.wireOp",EDGE,"E21")])],"isStart":false});
            var Q33;
            Q33=makeQuery(id+"F21.opExtrude","CAP_EDGE",EDGE,{"disambiguationData":[OSD([sQuery(id+"F0.wireOp",EDGE,"E22")])],"isStart":false});
            var Q34;
            Q34=makeQuery(id+"F21.opExtrude","CAP_EDGE",EDGE,{"disambiguationData":[OSD([sQuery(id+"F0.wireOp",EDGE,"E23")])],"isStart":false});
            var Q35;
            Q35=makeQuery(id+"F21.opExtrude","CAP_EDGE",EDGE,{"disambiguationData":[OSD([sQuery(id+"F0.wireOp",EDGE,"E18")])],"isStart":true});
            var Q36;
            Q36=makeQuery(id+"F21.opExtrude","CAP_EDGE",EDGE,{"disambiguationData":[OSD([sQuery(id+"F0.wireOp",EDGE,"E29")])],"isStart":true});
            var Q37;
            Q37=makeQuery(id+"F21.opExtrude","CAP_EDGE",EDGE,{"disambiguationData":[OSD([sQuery(id+"F0.wireOp",EDGE,"E28")])],"isStart":true});
            var Q38;
            Q38=makeQuery(id+"F21.opExtrude","CAP_EDGE",EDGE,{"disambiguationData":[OSD([sQuery(id+"F0.wireOp",EDGE,"E27")])],"isStart":true});
            var Q39;
            Q39=makeQuery(id+"F21.opExtrude","CAP_EDGE",EDGE,{"disambiguationData":[OSD([sQuery(id+"F0.wireOp",EDGE,"E19")])],"isStart":true});
            var Q40;
            Q40=makeQuery(id+"F21.opExtrude","CAP_EDGE",EDGE,{"disambiguationData":[OSD([sQuery(id+"F0.wireOp",EDGE,"E20")])],"isStart":true});
            var Q41;
            Q41=makeQuery(id+"F21.opExtrude","CAP_EDGE",EDGE,{"disambiguationData":[OSD([sQuery(id+"F0.wireOp",EDGE,"E21")])],"isStart":true});
            var Q42;
            Q42=makeQuery(id+"F21.opExtrude","CAP_EDGE",EDGE,{"disambiguationData":[OSD([sQuery(id+"F0.wireOp",EDGE,"E26")])],"isStart":true});
            var Q43;
            Q43=makeQuery(id+"F21.opExtrude","CAP_EDGE",EDGE,{"disambiguationData":[OSD([sQuery(id+"F0.wireOp",EDGE,"E25")])],"isStart":true});
            var Q44;
            Q44=makeQuery(id+"F21.opExtrude","CAP_EDGE",EDGE,{"disambiguationData":[OSD([sQuery(id+"F0.wireOp",EDGE,"E22")])],"isStart":true});
            var Q45;
            Q45=makeQuery(id+"F21.opExtrude","CAP_EDGE",EDGE,{"disambiguationData":[OSD([sQuery(id+"F0.wireOp",EDGE,"E23")])],"isStart":true});
            var Q46;
            Q46=makeQuery(id+"F21.opExtrude","CAP_EDGE",EDGE,{"disambiguationData":[OSD([sQuery(id+"F0.wireOp",EDGE,"E24")])],"isStart":true});
            var Q47;
            Q47=makeQuery(id+"F21.opExtrude","CAP_EDGE",EDGE,{"disambiguationData":[OSD([sQuery(id+"F0.wireOp",EDGE,"E47.MirrorCS")])],"isStart":true});
            var Q48;
            Q48=makeQuery(id+"F21.opExtrude","CAP_EDGE",EDGE,{"disambiguationData":[OSD([sQuery(id+"F0.wireOp",EDGE,"E46.MirrorCS")])],"isStart":true});
            var Q49;
            Q49=makeQuery(id+"F21.opExtrude","CAP_EDGE",EDGE,{"disambiguationData":[OSD([sQuery(id+"F0.wireOp",EDGE,"E33.MirrorCS")])],"isStart":true});
            var Q50;
            Q50=makeQuery(id+"F21.opExtrude","CAP_EDGE",EDGE,{"disambiguationData":[OSD([sQuery(id+"F0.wireOp",EDGE,"E35.MirrorCS")])],"isStart":true});
            var Q51;
            Q51=makeQuery(id+"F21.opExtrude","CAP_EDGE",EDGE,{"disambiguationData":[OSD([sQuery(id+"F0.wireOp",EDGE,"E32.MirrorCS")])],"isStart":true});
            var Q52;
            Q52=makeQuery(id+"F21.opExtrude","CAP_EDGE",EDGE,{"disambiguationData":[OSD([sQuery(id+"F0.wireOp",EDGE,"E37.MirrorCS")])],"isStart":true});
            var Q53;
            Q53=makeQuery(id+"F21.opExtrude","CAP_EDGE",EDGE,{"disambiguationData":[OSD([sQuery(id+"F0.wireOp",EDGE,"E42.MirrorCS")])],"isStart":true});
            var Q54;
            Q54=makeQuery(id+"F21.opExtrude","CAP_EDGE",EDGE,{"disambiguationData":[OSD([sQuery(id+"F0.wireOp",EDGE,"E31.MirrorCS")])],"isStart":true});
            var Q55;
            Q55=makeQuery(id+"F21.opExtrude","CAP_EDGE",EDGE,{"disambiguationData":[OSD([sQuery(id+"F0.wireOp",EDGE,"E41.MirrorCS")])],"isStart":true});
            var Q56;
            Q56=makeQuery(id+"F21.opExtrude","CAP_EDGE",EDGE,{"disambiguationData":[OSD([sQuery(id+"F0.wireOp",EDGE,"E39.MirrorCS")])],"isStart":true});
            var Q57;
            Q57=makeQuery(id+"F21.opExtrude","CAP_EDGE",EDGE,{"disambiguationData":[OSD([sQuery(id+"F0.wireOp",EDGE,"E177")])],"isStart":true});
            var Q58;
            Q58=makeQuery(id+"F21.opExtrude","CAP_EDGE",EDGE,{"disambiguationData":[OSD([sQuery(id+"F0.wireOp",EDGE,"E174")])],"isStart":true});
            var Q59;
            Q59=makeQuery(id+"F21.opExtrude","CAP_EDGE",EDGE,{"disambiguationData":[OSD([sQuery(id+"F0.wireOp",EDGE,"E176")])],"isStart":true});
            var Q60;
            Q60=makeQuery(id+"F21.opExtrude","CAP_EDGE",EDGE,{"disambiguationData":[OSD([sQuery(id+"F0.wireOp",EDGE,"E46.MirrorCS")])],"isStart":false});
            var Q61;
            Q61=makeQuery(id+"F21.opExtrude","CAP_EDGE",EDGE,{"disambiguationData":[OSD([sQuery(id+"F0.wireOp",EDGE,"E47.MirrorCS")])],"isStart":false});
            var Q62;
            Q62=makeQuery(id+"F21.opExtrude","CAP_EDGE",EDGE,{"disambiguationData":[OSD([sQuery(id+"F0.wireOp",EDGE,"E35.MirrorCS")])],"isStart":false});
            var Q63;
            Q63=makeQuery(id+"F21.opExtrude","CAP_EDGE",EDGE,{"disambiguationData":[OSD([sQuery(id+"F0.wireOp",EDGE,"E33.MirrorCS")])],"isStart":false});
            var Q64;
            Q64=makeQuery(id+"F21.opExtrude","CAP_EDGE",EDGE,{"disambiguationData":[OSD([sQuery(id+"F0.wireOp",EDGE,"E37.MirrorCS")])],"isStart":false});
            var Q65;
            Q65=makeQuery(id+"F21.opExtrude","CAP_EDGE",EDGE,{"disambiguationData":[OSD([sQuery(id+"F0.wireOp",EDGE,"E32.MirrorCS")])],"isStart":false});
            var Q66;
            Q66=makeQuery(id+"F21.opExtrude","CAP_EDGE",EDGE,{"disambiguationData":[OSD([sQuery(id+"F0.wireOp",EDGE,"E31.MirrorCS")])],"isStart":false});
            var Q67;
            Q67=makeQuery(id+"F21.opExtrude","CAP_EDGE",EDGE,{"disambiguationData":[OSD([sQuery(id+"F0.wireOp",EDGE,"E42.MirrorCS")])],"isStart":false});
            var Q68;
            Q68=makeQuery(id+"F21.opExtrude","CAP_EDGE",EDGE,{"disambiguationData":[OSD([sQuery(id+"F0.wireOp",EDGE,"E41.MirrorCS")])],"isStart":false});
            var Q69;
            Q69=makeQuery(id+"F21.opExtrude","CAP_EDGE",EDGE,{"disambiguationData":[OSD([sQuery(id+"F0.wireOp",EDGE,"E39.MirrorCS")])],"isStart":false});
            var Q70;
            Q70=makeQuery(id+"F21.opExtrude","CAP_EDGE",EDGE,{"disambiguationData":[OSD([sQuery(id+"F0.wireOp",EDGE,"E177")])],"isStart":false});
            var Q71;
            Q71=makeQuery(id+"F21.opExtrude","CAP_EDGE",EDGE,{"disambiguationData":[OSD([sQuery(id+"F0.wireOp",EDGE,"E174")])],"isStart":false});
            var Q72;
            Q72=makeQuery(id+"F21.opExtrude","CAP_EDGE",EDGE,{"disambiguationData":[OSD([sQuery(id+"F0.wireOp",EDGE,"E176")])],"isStart":false});
            var Q73;
            Q73=makeQuery(id+"F21.opExtrude","CAP_EDGE",EDGE,{"disambiguationData":[OSD([sQuery(id+"F0.wireOp",EDGE,"E175")])],"isStart":false});
            var Q74;
            Q74=makeQuery(id+"F21.opExtrude","CAP_EDGE",EDGE,{"disambiguationData":[OSD([sQuery(id+"F0.wireOp",EDGE,"E175")])],"isStart":true});
            var Q75;
            Q75=makeQuery(id+"F21.opExtrude","CAP_EDGE",EDGE,{"disambiguationData":[OSD([sQuery(id+"F0.wireOp",EDGE,"E44.MirrorCS")])],"isStart":true});
            var Q76;
            Q76=makeQuery(id+"F21.opExtrude","CAP_EDGE",EDGE,{"disambiguationData":[OSD([sQuery(id+"F0.wireOp",EDGE,"E45.MirrorCS")])],"isStart":true});
            var Q77;
            Q77=makeQuery(id+"F21.opExtrude","CAP_EDGE",EDGE,{"disambiguationData":[OSD([sQuery(id+"F0.wireOp",EDGE,"E36.MirrorCS")])],"isStart":true});
            var Q78;
            Q78=makeQuery(id+"F21.opExtrude","CAP_EDGE",EDGE,{"disambiguationData":[OSD([sQuery(id+"F0.wireOp",EDGE,"E40.MirrorCS")])],"isStart":true});
            var Q79;
            Q79=makeQuery(id+"F21.opExtrude","CAP_EDGE",EDGE,{"disambiguationData":[OSD([sQuery(id+"F0.wireOp",EDGE,"E43.MirrorCS")])],"isStart":true});
            var Q80;
            Q80=makeQuery(id+"F21.opExtrude","CAP_EDGE",EDGE,{"disambiguationData":[OSD([sQuery(id+"F0.wireOp",EDGE,"E34.MirrorCS")])],"isStart":true});
            var Q81;
            Q81=makeQuery(id+"F21.opExtrude","CAP_EDGE",EDGE,{"disambiguationData":[OSD([sQuery(id+"F0.wireOp",EDGE,"E38.MirrorCS")])],"isStart":true});
            var Q82;
            Q82=makeQuery(id+"F21.opExtrude","CAP_EDGE",EDGE,{"disambiguationData":[OSD([sQuery(id+"F0.wireOp",EDGE,"E30.MirrorCS")])],"isStart":true});
            var Q83;
            Q83=makeQuery(id+"F21.opExtrude","CAP_EDGE",EDGE,{"disambiguationData":[OSD([sQuery(id+"F0.wireOp",EDGE,"E188")])],"isStart":true});
            var Q84;
            Q84=makeQuery(id+"F21.opExtrude","CAP_EDGE",EDGE,{"disambiguationData":[OSD([sQuery(id+"F0.wireOp",EDGE,"E191")])],"isStart":true});
            var Q85;
            Q85=makeQuery(id+"F21.opExtrude","CAP_EDGE",EDGE,{"disambiguationData":[OSD([sQuery(id+"F0.wireOp",EDGE,"E189")])],"isStart":true});
            var Q86;
            Q86=makeQuery(id+"F21.opExtrude","CAP_EDGE",EDGE,{"disambiguationData":[OSD([sQuery(id+"F0.wireOp",EDGE,"E45.MirrorCS")])],"isStart":false});
            var Q87;
            Q87=makeQuery(id+"F21.opExtrude","CAP_EDGE",EDGE,{"disambiguationData":[OSD([sQuery(id+"F0.wireOp",EDGE,"E40.MirrorCS")])],"isStart":false});
            var Q88;
            Q88=makeQuery(id+"F21.opExtrude","CAP_EDGE",EDGE,{"disambiguationData":[OSD([sQuery(id+"F0.wireOp",EDGE,"E43.MirrorCS")])],"isStart":false});
            var Q89;
            Q89=makeQuery(id+"F21.opExtrude","CAP_EDGE",EDGE,{"disambiguationData":[OSD([sQuery(id+"F0.wireOp",EDGE,"E44.MirrorCS")])],"isStart":false});
            var Q90;
            Q90=makeQuery(id+"F21.opExtrude","CAP_EDGE",EDGE,{"disambiguationData":[OSD([sQuery(id+"F0.wireOp",EDGE,"E36.MirrorCS")])],"isStart":false});
            var Q91;
            Q91=makeQuery(id+"F21.opExtrude","CAP_EDGE",EDGE,{"disambiguationData":[OSD([sQuery(id+"F0.wireOp",EDGE,"E34.MirrorCS")])],"isStart":false});
            var Q92;
            Q92=makeQuery(id+"F21.opExtrude","CAP_EDGE",EDGE,{"disambiguationData":[OSD([sQuery(id+"F0.wireOp",EDGE,"E38.MirrorCS")])],"isStart":false});
            var Q93;
            Q93=makeQuery(id+"F21.opExtrude","CAP_EDGE",EDGE,{"disambiguationData":[OSD([sQuery(id+"F0.wireOp",EDGE,"E30.MirrorCS")])],"isStart":false});
            var Q94;
            Q94=makeQuery(id+"F21.opExtrude","CAP_EDGE",EDGE,{"disambiguationData":[OSD([sQuery(id+"F0.wireOp",EDGE,"E191")])],"isStart":false});
            var Q95;
            Q95=makeQuery(id+"F21.opExtrude","CAP_EDGE",EDGE,{"disambiguationData":[OSD([sQuery(id+"F0.wireOp",EDGE,"E188")])],"isStart":false});
            var Q96;
            Q96=makeQuery(id+"F21.opExtrude","CAP_EDGE",EDGE,{"disambiguationData":[OSD([sQuery(id+"F0.wireOp",EDGE,"E189")])],"isStart":false});
            fillet(context, id + "F22", {"entities" : qUnion([Q0, Q1, Q2, Q3, Q4, Q5, Q6, Q7, Q8, Q9, Q10, Q11, Q12, Q13, Q14, Q15, Q16, Q17, Q18, Q19, Q20, Q21, Q22, Q23, Q24, Q25, Q26, Q27, Q28, Q29, Q30, Q31, Q32, Q33, Q34, Q35, Q36, Q37, Q38, Q39, Q40, Q41, Q42, Q43, Q44, Q45, Q46, Q47, Q48, Q49, Q50, Q51, Q52, Q53, Q54, Q55, Q56, Q57, Q58, Q59, Q60, Q61, Q62, Q63, Q64, Q65, Q66, Q67, Q68, Q69, Q70, Q71, Q72, Q73, Q74, Q75, Q76, Q77, Q78, Q79, Q80, Q81, Q82, Q83, Q84, Q85, Q86, Q87, Q88, Q89, Q90, Q91, Q92, Q93, Q94, Q95, Q96]), "radius" : 1.52 * mm, "tangentPropagation" : true, "allowEdgeOverflow" : false});
        }
    });
